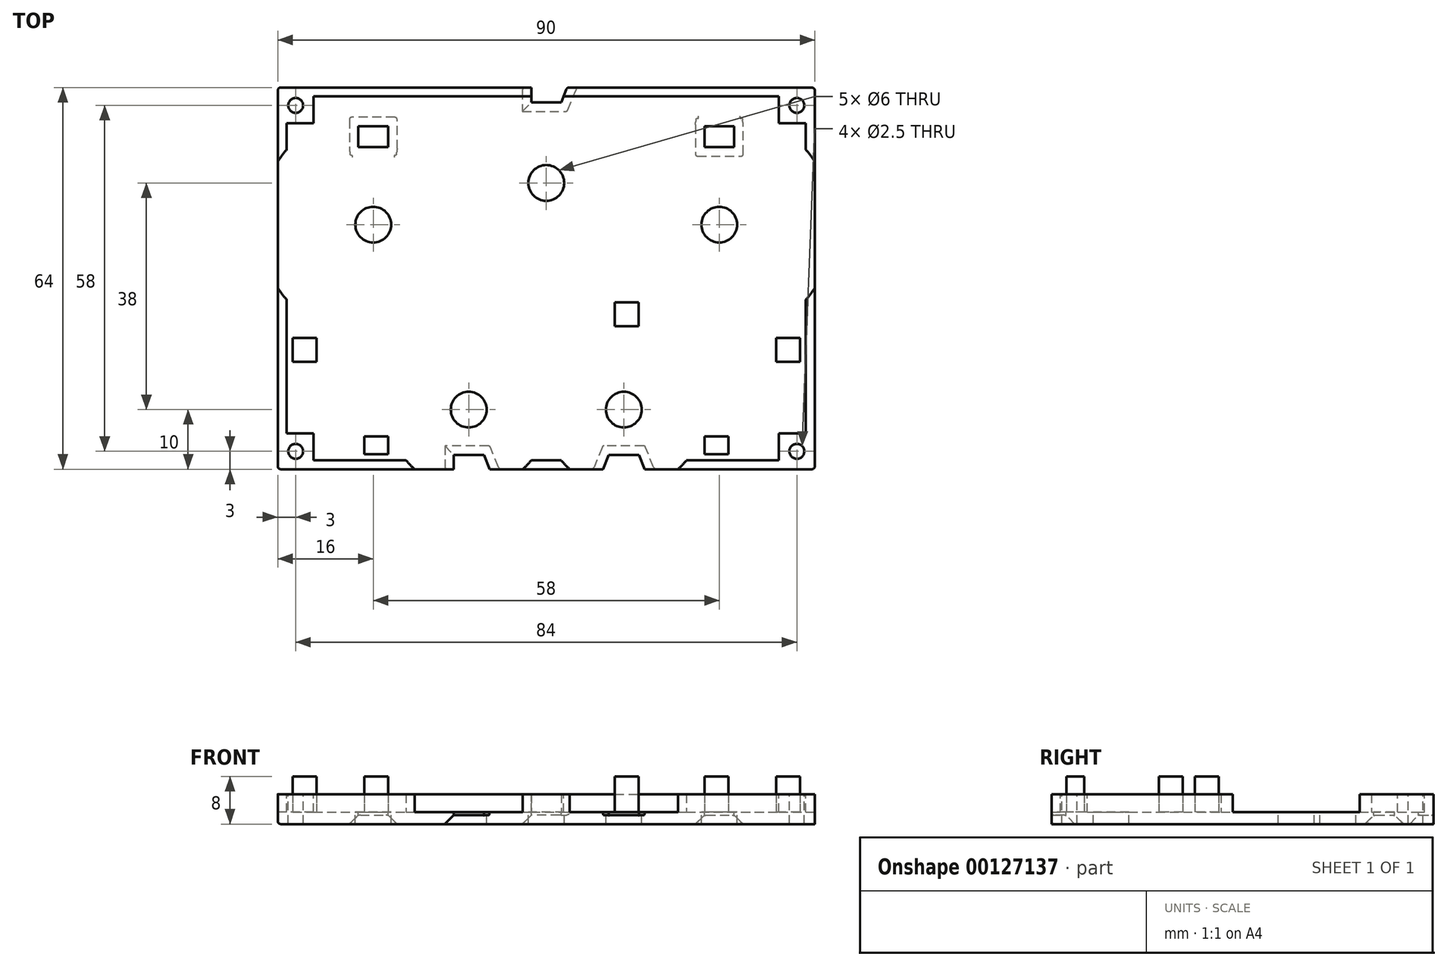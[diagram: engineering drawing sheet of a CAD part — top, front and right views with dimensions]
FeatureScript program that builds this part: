
annotation { "Feature Type Name" : "Feature", "Feature Type Description" : "" }
export const myFeature = defineFeature(function(context is Context, id is Id, definition is map)
    precondition{}
    {
        {
            var Q0;
            Q0=qCreatedBy(makeId("Top.planeOp"),FACE);
            var sketch = newSketch(context, id + "F0", { "sketchPlane" : qUnion([Q0])});
            skLineSegment(sketch, "E0.bottom", {"start": v(0, 0) * mm, "end": v(90, 0) * mm});
            skLineSegment(sketch, "E0.top", {"start": v(0, 64) * mm, "end": v(90, 64) * mm});
            skLineSegment(sketch, "E0.left", {"start": v(0, 0) * mm, "end": v(0, 64) * mm});
            skLineSegment(sketch, "E0.right", {"start": v(90, 0) * mm, "end": v(90, 64) * mm});
            skSolve(sketch);
        }
        {
            var Q0;
            Q0=makeQuery(id+"F0.imprint","IMPRINT",FACE,{"disambiguationData":[TD([[makeQuery(id+"F0.imprint","IMPRINT",EDGE,{"derivedFrom":sQuery(id+"F0.wireOp",EDGE,"E0.bottom")}),1.0]])]});
            extrude(context, id + "F1", {"entities" : qUnion([Q0]), "depth" : 2 * mm});
        }
        {
            var Q0;
            Q0=makeQuery(id+"F1.opExtrude","CAP_FACE",FACE,{"disambiguationData":[OSD([sQuery(id+"F0.wireOp",EDGE,"E0.bottom"),sQuery(id+"F0.wireOp",EDGE,"E0.top"),sQuery(id+"F0.wireOp",EDGE,"E0.left"),sQuery(id+"F0.wireOp",EDGE,"E0.right")])],"isStart":false});
            var sketch = newSketch(context, id + "F2", { "sketchPlane" : qUnion([Q0])});
            skCircle(sketch, "E1", {"center": v(16, 41) * mm, "radius": 18.2 * mm, "construction": true});
            skCircle(sketch, "E2", {"center": v(45, 48) * mm, "radius": 18.2 * mm, "construction": true});
            skCircle(sketch, "E3", {"center": v(74, 41) * mm, "radius": 18.2 * mm, "construction": true});
            skLineSegment(sketch, "E4", {"start": v(45, 64) * mm, "end": v(45, 0) * mm, "construction": true});
            skLineSegment(sketch, "E5", {"start": v(0, 41) * mm, "end": v(90, 41) * mm, "construction": true});
            skCircle(sketch, "E6", {"center": v(16, 41) * mm, "radius": 3 * mm, "construction": true});
            skCircle(sketch, "E7", {"center": v(45, 48) * mm, "radius": 3 * mm, "construction": true});
            skCircle(sketch, "E8", {"center": v(74, 41) * mm, "radius": 3 * mm, "construction": true});
            skCircle(sketch, "E9", {"center": v(32, 10) * mm, "radius": 12.5 * mm, "construction": true});
            skCircle(sketch, "E10", {"center": v(58, 10) * mm, "radius": 12.5 * mm, "construction": true});
            skLineSegment(sketch, "E11", {"start": v(32, 10) * mm, "end": v(58, 10) * mm, "construction": true});
            skPoint(sketch, "E12", {"position": v(45, 10) * mm});
            skSolve(sketch);
        }
        {
            var Q0;
            Q0=makeQuery(id+"F2.imprint","IMPRINT",FACE,{"disambiguationData":[TD([[makeQuery(id+"F2.imprint","IMPRINT",EDGE,{"derivedFrom":makeQuery(id+"F1.opExtrude","CAP_EDGE",EDGE,{"disambiguationData":[OSD([sQuery(id+"F0.wireOp",EDGE,"E0.bottom")])],"isStart":false})}),1.0]])]});
            var sketch = newSketch(context, id + "F3", { "sketchPlane" : qUnion([Q0])});
            skLineSegment(sketch, "E13.0", {"start": v(0, 0) * mm, "end": v(0, 64) * mm});
            skLineSegment(sketch, "E14.0", {"start": v(0, 0) * mm, "end": v(90, 0) * mm});
            skLineSegment(sketch, "E15.0", {"start": v(90, 0) * mm, "end": v(90, 64) * mm});
            skLineSegment(sketch, "E16.0", {"start": v(0, 64) * mm, "end": v(90, 64) * mm});
            skLineSegment(sketch, "E17.0", {"start": v(1.5, 62.5) * mm, "end": v(88.5, 62.5) * mm});
            skLineSegment(sketch, "E18.0", {"start": v(1.5, 1.5) * mm, "end": v(1.5, 62.5) * mm});
            skLineSegment(sketch, "E19.0", {"start": v(1.5, 1.5) * mm, "end": v(88.5, 1.5) * mm});
            skLineSegment(sketch, "E20.0", {"start": v(88.5, 1.5) * mm, "end": v(88.5, 62.5) * mm});
            skSolve(sketch);
        }
        {
            var Q0;
            Q0=makeQuery(id+"F3.imprint","IMPRINT",FACE,{"disambiguationData":[TD([[makeQuery(id+"F3.imprint","IMPRINT",EDGE,{"derivedFrom":sQuery(id+"F3.wireOp",EDGE,"E13.0")}),-1.0]])]});
            extrude(context, id + "F4", {"entities" : qUnion([Q0]), "operationType" : NewBodyOperationType.ADD, "depth" : 3 * mm});
        }
        {
            var Q0;
            Q0=makeQuery(id+"F2.imprint","IMPRINT",FACE,{"disambiguationData":[TD([[makeQuery(id+"F2.imprint","IMPRINT",EDGE,{"derivedFrom":makeQuery(id+"F1.opExtrude","CAP_EDGE",EDGE,{"disambiguationData":[OSD([sQuery(id+"F0.wireOp",EDGE,"E0.bottom")])],"isStart":false})}),1.0]])]});
            var sketch = newSketch(context, id + "F5", { "sketchPlane" : qUnion([Q0])});
            skCircle(sketch, "E21.0", {"center": v(16, 41) * mm, "radius": 19.2 * mm});
            skCircle(sketch, "E22.0", {"center": v(74, 41) * mm, "radius": 19.2 * mm});
            skCircle(sketch, "E23.0", {"center": v(32, 10) * mm, "radius": 13.5 * mm});
            skCircle(sketch, "E24.0", {"center": v(58, 10) * mm, "radius": 13.5 * mm});
            skSolve(sketch);
        }
        {
            var Q0;
            {var subQ0=sQuery(id+"F5.wireOp",EDGE,"E22.0");var subQ1=makeQuery(id+"F2.imprint","IMPRINT",EDGE,{"derivedFrom":makeQuery(id+"F1.opExtrude","CAP_EDGE",EDGE,{"disambiguationData":[OSD([sQuery(id+"F0.wireOp",EDGE,"E0.right")])],"isStart":false})});var subQ2=makeQuery(id+"F5.imprint","INTERSECT",VERTEX,{"disambiguationData":[OD(0.0)],"derivedFrom":[subQ1,subQ0]});Q0=makeQuery(id+"F5.imprint","IMPRINT",FACE,{"disambiguationData":[TD([[makeQuery(id+"F5.imprint","IMPRINT",EDGE,{"disambiguationData":[TD([[subQ2,1.0]])],"derivedFrom":subQ0}),1.0]])]});}
            var Q1;
            {var subQ0=sQuery(id+"F5.wireOp",EDGE,"E21.0");var subQ1=makeQuery(id+"F2.imprint","IMPRINT",EDGE,{"derivedFrom":makeQuery(id+"F1.opExtrude","CAP_EDGE",EDGE,{"disambiguationData":[OSD([sQuery(id+"F0.wireOp",EDGE,"E0.left")])],"isStart":false})});var subQ2=makeQuery(id+"F5.imprint","INTERSECT",VERTEX,{"disambiguationData":[OD(0.0)],"derivedFrom":[subQ1,subQ0]});Q1=makeQuery(id+"F5.imprint","IMPRINT",FACE,{"disambiguationData":[TD([[makeQuery(id+"F5.imprint","IMPRINT",EDGE,{"disambiguationData":[TD([[subQ2,-1.0]])],"derivedFrom":subQ0}),1.0]])]});}
            var Q2;
            {var subQ0=sQuery(id+"F5.wireOp",EDGE,"E23.0");var subQ1=makeQuery(id+"F2.imprint","IMPRINT",EDGE,{"derivedFrom":makeQuery(id+"F1.opExtrude","CAP_EDGE",EDGE,{"disambiguationData":[OSD([sQuery(id+"F0.wireOp",EDGE,"E0.bottom")])],"isStart":false})});var subQ2=makeQuery(id+"F5.imprint","INTERSECT",VERTEX,{"disambiguationData":[OD(0.0)],"derivedFrom":[subQ1,subQ0]});Q2=makeQuery(id+"F5.imprint","IMPRINT",FACE,{"disambiguationData":[TD([[makeQuery(id+"F5.imprint","IMPRINT",EDGE,{"disambiguationData":[TD([[subQ2,1.0]])],"derivedFrom":subQ0}),1.0]])]});}
            var Q3;
            {var subQ0=sQuery(id+"F5.wireOp",EDGE,"E23.0");var subQ1=makeQuery(id+"F2.imprint","IMPRINT",EDGE,{"derivedFrom":makeQuery(id+"F1.opExtrude","CAP_EDGE",EDGE,{"disambiguationData":[OSD([sQuery(id+"F0.wireOp",EDGE,"E0.bottom")])],"isStart":false})});var subQ2=makeQuery(id+"F5.imprint","INTERSECT",VERTEX,{"disambiguationData":[OD(0.0)],"derivedFrom":[subQ1,subQ0]});Q3=makeQuery(id+"F5.imprint","IMPRINT",FACE,{"disambiguationData":[TD([[makeQuery(id+"F5.imprint","IMPRINT",EDGE,{"disambiguationData":[TD([[subQ2,-1.0]])],"derivedFrom":subQ0}),1.0]])]});}
            var Q4;
            {var subQ0=sQuery(id+"F5.wireOp",EDGE,"E24.0");var subQ1=sQuery(id+"F5.wireOp",EDGE,"E23.0");var subQ2=makeQuery(id+"F5.imprint","INTERSECT",VERTEX,{"disambiguationData":[OD(0.0)],"derivedFrom":[subQ1,subQ0]});Q4=makeQuery(id+"F5.imprint","IMPRINT",FACE,{"disambiguationData":[TD([[makeQuery(id+"F5.imprint","IMPRINT",EDGE,{"disambiguationData":[TD([[subQ2,1.0]])],"derivedFrom":subQ1}),-1.0]])]});}
            extrude(context, id + "F6", {"entities" : qUnion([Q0, Q1, Q2, Q3, Q4]), "operationType" : NewBodyOperationType.REMOVE, "endBound" : BoundingType.THROUGH_ALL, "depth" : 25 * mm});
        }
        {
            var Q0;
            Q0=makeQuery(id+"F2.imprint","IMPRINT",FACE,{"disambiguationData":[TD([[makeQuery(id+"F2.imprint","IMPRINT",EDGE,{"derivedFrom":makeQuery(id+"F1.opExtrude","CAP_EDGE",EDGE,{"disambiguationData":[OSD([sQuery(id+"F0.wireOp",EDGE,"E0.bottom")])],"isStart":false})}),1.0]])]});
            var sketch = newSketch(context, id + "F7", { "sketchPlane" : qUnion([Q0])});
            skCircle(sketch, "E25", {"center": v(16, 41) * mm, "radius": 3 * mm});
            skCircle(sketch, "E26", {"center": v(45, 48) * mm, "radius": 3 * mm});
            skCircle(sketch, "E27", {"center": v(74, 41) * mm, "radius": 3 * mm});
            skCircle(sketch, "E28", {"center": v(32, 10) * mm, "radius": 3 * mm});
            skCircle(sketch, "E29", {"center": v(58, 10) * mm, "radius": 3 * mm});
            skSolve(sketch);
        }
        {
            var Q0;
            Q0=makeQuery(id+"F7.imprint","IMPRINT",FACE,{"disambiguationData":[TD([[makeQuery(id+"F7.imprint","IMPRINT",EDGE,{"derivedFrom":sQuery(id+"F7.wireOp",EDGE,"E26")}),1.0]])]});
            var Q1;
            Q1=makeQuery(id+"F7.imprint","IMPRINT",FACE,{"disambiguationData":[TD([[makeQuery(id+"F7.imprint","IMPRINT",EDGE,{"derivedFrom":sQuery(id+"F7.wireOp",EDGE,"E25")}),1.0]])]});
            var Q2;
            Q2=makeQuery(id+"F7.imprint","IMPRINT",FACE,{"disambiguationData":[TD([[makeQuery(id+"F7.imprint","IMPRINT",EDGE,{"derivedFrom":sQuery(id+"F7.wireOp",EDGE,"E27")}),1.0]])]});
            extrude(context, id + "F8", {"entities" : qUnion([Q0, Q1, Q2]), "operationType" : NewBodyOperationType.REMOVE, "endBound" : BoundingType.THROUGH_ALL, "oppositeDirection" : true, "depth" : 25 * mm});
        }
        {
            var Q0;
            Q0=makeQuery(id+"F7.imprint","IMPRINT",FACE,{"disambiguationData":[TD([[makeQuery(id+"F7.imprint","IMPRINT",EDGE,{"derivedFrom":sQuery(id+"F7.wireOp",EDGE,"E28")}),1.0]])]});
            var Q1;
            Q1=makeQuery(id+"F7.imprint","IMPRINT",FACE,{"disambiguationData":[TD([[makeQuery(id+"F7.imprint","IMPRINT",EDGE,{"derivedFrom":sQuery(id+"F7.wireOp",EDGE,"E29")}),1.0]])]});
            extrude(context, id + "F9", {"entities" : qUnion([Q0, Q1]), "operationType" : NewBodyOperationType.REMOVE, "endBound" : BoundingType.THROUGH_ALL, "oppositeDirection" : true, "depth" : 25 * mm});
        }
        {
            var Q0;
            Q0=makeQuery(id+"F2.imprint","IMPRINT",FACE,{"disambiguationData":[TD([[makeQuery(id+"F2.imprint","IMPRINT",EDGE,{"derivedFrom":makeQuery(id+"F1.opExtrude","CAP_EDGE",EDGE,{"disambiguationData":[OSD([sQuery(id+"F0.wireOp",EDGE,"E0.bottom")])],"isStart":false})}),1.0]])]});
            var sketch = newSketch(context, id + "F10", { "sketchPlane" : qUnion([Q0])});
            skLineSegment(sketch, "E30", {"start": v(76, 10) * mm, "end": v(58, 10) * mm, "construction": true});
            skPoint(sketch, "E31", {"position": v(19.5, 10) * mm});
            skPoint(sketch, "E32", {"position": v(70.5, 10) * mm});
            skLineSegment(sketch, "E33", {"start": v(45, 48) * mm, "end": v(45, 21.8) * mm, "construction": true});
            skPoint(sketch, "E34", {"position": v(45, 29.8) * mm});
            skLineSegment(sketch, "E35.bottom", {"start": v(42.5, 21.8) * mm, "end": v(47.5, 21.8) * mm});
            skLineSegment(sketch, "E35.top", {"start": v(42.5, 19.3) * mm, "end": v(47.5, 19.3) * mm, "construction": true});
            skLineSegment(sketch, "E35.left", {"start": v(42.5, 21.8) * mm, "end": v(42.5, 19.3) * mm});
            skLineSegment(sketch, "E35.right", {"start": v(47.5, 21.8) * mm, "end": v(47.5, 19.3) * mm});
            skLineSegment(sketch, "E36", {"start": v(45, 21.8) * mm, "end": v(45, 16.8) * mm, "construction": true});
            skPoint(sketch, "E36.endSnap0", {"position": v(45, 21.8) * mm});
            skLineSegment(sketch, "E37", {"start": v(45, 16.8) * mm, "end": v(47.5, 19.3) * mm});
            skLineSegment(sketch, "E38", {"start": v(42.5, 19.3) * mm, "end": v(45, 16.8) * mm});
            skLineSegment(sketch, "E39.bottom", {"start": v(44.5, 21.8) * mm, "end": v(45.5, 21.8) * mm});
            skLineSegment(sketch, "E39.top", {"start": v(44.5, 17.3) * mm, "end": v(45.5, 17.3) * mm});
            skLineSegment(sketch, "E39.left", {"start": v(44.5, 21.8) * mm, "end": v(44.5, 17.3) * mm});
            skLineSegment(sketch, "E39.right", {"start": v(45.5, 21.8) * mm, "end": v(45.5, 17.3) * mm});
            skLineSegment(sketch, "E40.0.0", {"start": v(0, 64) * mm, "end": v(0, 0) * mm, "construction": true});
            skLineSegment(sketch, "E40.0.1", {"start": v(0, 0) * mm, "end": v(90, 0) * mm, "construction": true});
            skLineSegment(sketch, "E40.0.2", {"start": v(90, 0) * mm, "end": v(90, 64) * mm, "construction": true});
            skLineSegment(sketch, "E40.0.3", {"start": v(90, 64) * mm, "end": v(0, 64) * mm, "construction": true});
            skLineSegment(sketch, "E41.0", {"start": v(1.5, 62.5) * mm, "end": v(88.5, 62.5) * mm, "construction": true});
            skLineSegment(sketch, "E42.bottom", {"start": v(80.5, 12.82) * mm, "end": v(85.5, 12.82) * mm, "construction": true});
            skLineSegment(sketch, "E42.top", {"start": v(80.5, 10.5) * mm, "end": v(85.5, 10.5) * mm});
            skLineSegment(sketch, "E42.left", {"start": v(80.5, 12.82) * mm, "end": v(80.5, 10.5) * mm});
            skLineSegment(sketch, "E42.right", {"start": v(85.5, 12.82) * mm, "end": v(85.5, 10.5) * mm, "construction": true});
            skLineSegment(sketch, "E43.MirrorCS", {"start": v(85.5, 7.18) * mm, "end": v(85.5, 9.5) * mm});
            skLineSegment(sketch, "E44.MirrorCS", {"start": v(80.5, 7.18) * mm, "end": v(80.5, 9.5) * mm});
            skLineSegment(sketch, "E45.MirrorCS", {"start": v(80.5, 7.18) * mm, "end": v(85.5, 7.18) * mm});
            skLineSegment(sketch, "E46.MirrorCS", {"start": v(80.5, 9.5) * mm, "end": v(85.5, 9.5) * mm});
            skLineSegment(sketch, "E47", {"start": v(74, 41) * mm, "end": v(83.82, 14.03) * mm, "construction": true});
            skPoint(sketch, "E48", {"position": v(80.22, 23.9) * mm});
            skPoint(sketch, "E49.endSnap0", {"position": v(47.5, 20.55) * mm});
            skLineSegment(sketch, "E50", {"start": v(83.35, 13.86) * mm, "end": v(88.5, 15.74) * mm, "construction": true});
            skLineSegment(sketch, "E51.0", {"start": v(88.5, 1.5) * mm, "end": v(88.5, 28.41) * mm, "construction": true});
            skLineSegment(sketch, "E52", {"start": v(84.29, 14.2) * mm, "end": v(88.5, 15.74) * mm});
            skLineSegment(sketch, "E53", {"start": v(88.5, 15.74) * mm, "end": v(88.5, 3.62) * mm});
            skLineSegment(sketch, "E54", {"start": v(83.35, 13.86) * mm, "end": v(84.57, 10.5) * mm});
            skLineSegment(sketch, "E55", {"start": v(83.35, 13.86) * mm, "end": v(80.5, 12.82) * mm});
            skLineSegment(sketch, "E56", {"start": v(84.57, 10.5) * mm, "end": v(85.5, 10.5) * mm});
            skLineSegment(sketch, "E57.MirrorCS", {"start": v(0, 0) * mm, "end": v(0, 64) * mm, "construction": true});
            skPoint(sketch, "E58.MirrorP", {"position": v(9.78, 23.9) * mm});
            skLineSegment(sketch, "E59", {"start": v(88.5, 10.5) * mm, "end": v(85.63, 10.5) * mm});
            skLineSegment(sketch, "E60", {"start": v(84.29, 14.2) * mm, "end": v(85.63, 10.5) * mm});
            skLineSegment(sketch, "E61", {"start": v(88.25, 15.64) * mm, "end": v(88.25, 10.5) * mm});
            skLineSegment(sketch, "E62.MirrorCS", {"start": v(5.43, 10.5) * mm, "end": v(4.5, 10.5) * mm});
            skLineSegment(sketch, "E63.MirrorCS", {"start": v(5.71, 14.2) * mm, "end": v(1.5, 15.74) * mm});
            skLineSegment(sketch, "E64.MirrorCS", {"start": v(1.5, 15.74) * mm, "end": v(1.5, 3.62) * mm});
            skLineSegment(sketch, "E65.MirrorCS", {"start": v(16, 41) * mm, "end": v(6.18, 14.03) * mm, "construction": true});
            skLineSegment(sketch, "E66.MirrorCS", {"start": v(6.65, 13.86) * mm, "end": v(9.5, 12.82) * mm});
            skLineSegment(sketch, "E67.MirrorCS", {"start": v(6.65, 13.86) * mm, "end": v(1.5, 15.74) * mm, "construction": true});
            skLineSegment(sketch, "E68.MirrorCS", {"start": v(9.5, 7.18) * mm, "end": v(4.5, 7.18) * mm});
            skLineSegment(sketch, "E69.MirrorCS", {"start": v(9.5, 10.5) * mm, "end": v(4.5, 10.5) * mm});
            skLineSegment(sketch, "E70.MirrorCS", {"start": v(5.71, 14.2) * mm, "end": v(4.37, 10.5) * mm});
            skLineSegment(sketch, "E71.MirrorCS", {"start": v(9.5, 12.82) * mm, "end": v(9.5, 10.5) * mm});
            skLineSegment(sketch, "E72.MirrorCS", {"start": v(9.5, 7.18) * mm, "end": v(9.5, 9.5) * mm});
            skLineSegment(sketch, "E73.MirrorCS", {"start": v(1.5, 1.5) * mm, "end": v(1.5, 28.41) * mm, "construction": true});
            skLineSegment(sketch, "E74.MirrorCS", {"start": v(1.75, 15.64) * mm, "end": v(1.75, 10.5) * mm});
            skLineSegment(sketch, "E75.MirrorCS", {"start": v(4.5, 12.82) * mm, "end": v(4.5, 10.5) * mm, "construction": true});
            skLineSegment(sketch, "E76.MirrorCS", {"start": v(90, 0) * mm, "end": v(0, 0) * mm, "construction": true});
            skLineSegment(sketch, "E77.MirrorCS", {"start": v(14, 10) * mm, "end": v(32, 10) * mm, "construction": true});
            skLineSegment(sketch, "E78.MirrorCS", {"start": v(9.5, 12.82) * mm, "end": v(4.5, 12.82) * mm, "construction": true});
            skLineSegment(sketch, "E79.MirrorCS", {"start": v(6.65, 13.86) * mm, "end": v(5.43, 10.5) * mm});
            skLineSegment(sketch, "E80.MirrorCS", {"start": v(4.5, 7.18) * mm, "end": v(4.5, 9.5) * mm});
            skLineSegment(sketch, "E81.MirrorCS", {"start": v(9.5, 9.5) * mm, "end": v(4.5, 9.5) * mm});
            skLineSegment(sketch, "E82.MirrorCS", {"start": v(1.5, 10.5) * mm, "end": v(4.37, 10.5) * mm});
            skSolve(sketch);
        }
        {
            var Q0;
            {var subQ0=sQuery(id+"F3.wireOp",EDGE,"E14.0");var subQ1=sQuery(id+"F3.wireOp",EDGE,"E13.0");var subQ2=sQuery(id+"F3.wireOp",EDGE,"E18.0");var subQ3=sQuery(id+"F0.wireOp",EDGE,"E0.bottom");var subQ4=sQuery(id+"F3.wireOp",EDGE,"E19.0");var subQ5=sQuery(id+"F5.wireOp",EDGE,"E24.0");var subQ6=sQuery(id+"F5.wireOp",EDGE,"E23.0");var subQ7=makeQuery(id+"F2.imprint","IMPRINT",EDGE,{"derivedFrom":makeQuery(id+"F1.opExtrude","CAP_EDGE",EDGE,{"disambiguationData":[OSD([subQ3])],"isStart":false})});var subQ9=makeQuery(id+"F5.imprint","INTERSECT",VERTEX,{"disambiguationData":[OD(0.0)],"derivedFrom":[subQ7,subQ6]});Q0=makeQuery(id+"F6.boolean.opBoolean","SPLIT",FACE,{"disambiguationData":[TD([makeQuery(id+"F1.opExtrude","SWEPT_FACE",FACE,{"disambiguationData":[OSD([subQ3])]}),makeQuery(id+"F1.opExtrude","SWEPT_FACE",FACE,{"disambiguationData":[OSD([sQuery(id+"F0.wireOp",EDGE,"E0.left")])]}),makeQuery(id+"F4.opExtrude","SWEPT_FACE",FACE,{"disambiguationData":[OSD([subQ1])]}),makeQuery(id+"F4.opExtrude","SWEPT_FACE",FACE,{"disambiguationData":[OSD([subQ0])]}),makeQuery(id+"F4.opExtrude","SWEPT_FACE",FACE,{"disambiguationData":[OSD([subQ2])]}),makeQuery(id+"F4.opExtrude","SWEPT_FACE",FACE,{"disambiguationData":[OSD([subQ4])]}),makeQuery(id+"F6.opExtrude","SWEPT_FACE",FACE,{"disambiguationData":[OSD([sQuery(id+"F5.wireOp",EDGE,"E21.0")])]}),makeQuery(id+"F6.opExtrude","SWEPT_FACE",FACE,{"disambiguationData":[OSD([subQ6]),TDD([makeQuery(id+"F5.imprint","IMPRINT",EDGE,{"disambiguationData":[TD([[makeQuery(id+"F5.imprint","INTERSECT",VERTEX,{"disambiguationData":[OD(0.0)],"derivedFrom":[subQ6,subQ5]}),-1.0]])],"derivedFrom":subQ6}),makeQuery(id+"F5.imprint","IMPRINT",EDGE,{"disambiguationData":[TD([[subQ9,-1.0]])],"derivedFrom":subQ6}),makeQuery(id+"F5.imprint","IMPRINT",EDGE,{"disambiguationData":[TD([[makeQuery(id+"F5.imprint","INTERSECT",VERTEX,{"disambiguationData":[OD(1.0)],"derivedFrom":[subQ6,subQ5]}),1.0]])],"derivedFrom":subQ6})])]})])],"derivedFrom":makeQuery(id+"F4.opExtrude","CAP_FACE",FACE,{"disambiguationData":[OSD([subQ1,subQ0,sQuery(id+"F3.wireOp",EDGE,"E15.0"),sQuery(id+"F3.wireOp",EDGE,"E16.0"),sQuery(id+"F3.wireOp",EDGE,"E17.0"),subQ2,subQ4,sQuery(id+"F3.wireOp",EDGE,"E20.0")])],"isStart":false})});}
            var sketch = newSketch(context, id + "F11", { "sketchPlane" : qUnion([Q0])});
            skLineSegment(sketch, "E83.0", {"start": v(1.5, 1.5) * mm, "end": v(1.5, 28.41) * mm});
            skLineSegment(sketch, "E83.1", {"start": v(1.5, 1.5) * mm, "end": v(21.51, 1.5) * mm});
            skLineSegment(sketch, "E83.2", {"start": v(88.5, 53.59) * mm, "end": v(88.5, 62.5) * mm});
            skLineSegment(sketch, "E83.3", {"start": v(1.5, 62.5) * mm, "end": v(88.5, 62.5) * mm});
            skLineSegment(sketch, "E83.4", {"start": v(1.5, 53.59) * mm, "end": v(1.5, 62.5) * mm});
            skLineSegment(sketch, "E83.5", {"start": v(88.5, 1.5) * mm, "end": v(88.5, 28.41) * mm});
            skLineSegment(sketch, "E83.6", {"start": v(68.49, 1.5) * mm, "end": v(88.5, 1.5) * mm});
            skLineSegment(sketch, "E84.bottom", {"start": v(1.5, 1.5) * mm, "end": v(6, 1.5) * mm});
            skLineSegment(sketch, "E84.top", {"start": v(1.5, 6) * mm, "end": v(6, 6) * mm});
            skLineSegment(sketch, "E84.left", {"start": v(1.5, 1.5) * mm, "end": v(1.5, 6) * mm});
            skLineSegment(sketch, "E84.right", {"start": v(6, 1.5) * mm, "end": v(6, 6) * mm});
            skLineSegment(sketch, "E85.bottom", {"start": v(1.5, 62.5) * mm, "end": v(6, 62.5) * mm});
            skLineSegment(sketch, "E85.top", {"start": v(1.5, 58) * mm, "end": v(6, 58) * mm});
            skLineSegment(sketch, "E85.left", {"start": v(1.5, 62.5) * mm, "end": v(1.5, 58) * mm});
            skLineSegment(sketch, "E85.right", {"start": v(6, 62.5) * mm, "end": v(6, 58) * mm});
            skLineSegment(sketch, "E86.bottom", {"start": v(88.5, 1.5) * mm, "end": v(84, 1.5) * mm});
            skLineSegment(sketch, "E86.top", {"start": v(88.5, 6) * mm, "end": v(84, 6) * mm});
            skLineSegment(sketch, "E86.left", {"start": v(88.5, 1.5) * mm, "end": v(88.5, 6) * mm});
            skLineSegment(sketch, "E86.right", {"start": v(84, 1.5) * mm, "end": v(84, 6) * mm});
            skLineSegment(sketch, "E87.bottom", {"start": v(88.5, 62.5) * mm, "end": v(84, 62.5) * mm});
            skLineSegment(sketch, "E87.top", {"start": v(88.5, 58) * mm, "end": v(84, 58) * mm});
            skLineSegment(sketch, "E87.left", {"start": v(88.5, 62.5) * mm, "end": v(88.5, 58) * mm});
            skLineSegment(sketch, "E87.right", {"start": v(84, 62.5) * mm, "end": v(84, 58) * mm});
            skCircle(sketch, "E88", {"center": v(3, 3) * mm, "radius": 1.25 * mm});
            skCircle(sketch, "E89", {"center": v(3, 61) * mm, "radius": 1.25 * mm});
            skCircle(sketch, "E90", {"center": v(87, 61) * mm, "radius": 1.25 * mm});
            skCircle(sketch, "E91", {"center": v(87, 3) * mm, "radius": 1.25 * mm});
            skSolve(sketch);
        }
        {
            var Q0;
            Q0 = qSketchRegion(id + "F11", true);
            extrude(context, id + "F12", {"entities" : qUnion([Q0]), "operationType" : NewBodyOperationType.ADD, "endBound" : BoundingType.UP_TO_NEXT, "oppositeDirection" : true, "depth" : 25 * mm});
        }
        {
            var Q0;
            {var subQ0=sQuery(id+"F3.wireOp",EDGE,"E20.0");var subQ1=sQuery(id+"F3.wireOp",EDGE,"E17.0");var subQ2=sQuery(id+"F3.wireOp",EDGE,"E15.0");var subQ3=sQuery(id+"F3.wireOp",EDGE,"E16.0");var subQ4=sQuery(id+"F3.wireOp",EDGE,"E18.0");var subQ5=sQuery(id+"F3.wireOp",EDGE,"E13.0");Q0=makeQuery(id+"F12.boolean.opBoolean","MERGE",FACE,{"derivedFrom":[makeQuery(id+"F6.boolean.opBoolean","SPLIT",FACE,{"disambiguationData":[TD([makeQuery(id+"F1.opExtrude","SWEPT_FACE",FACE,{"disambiguationData":[OSD([sQuery(id+"F0.wireOp",EDGE,"E0.top")])]}),makeQuery(id+"F1.opExtrude","SWEPT_FACE",FACE,{"disambiguationData":[OSD([sQuery(id+"F0.wireOp",EDGE,"E0.left")])]}),makeQuery(id+"F1.opExtrude","SWEPT_FACE",FACE,{"disambiguationData":[OSD([sQuery(id+"F0.wireOp",EDGE,"E0.right")])]}),makeQuery(id+"F4.opExtrude","SWEPT_FACE",FACE,{"disambiguationData":[OSD([subQ5])]}),makeQuery(id+"F4.opExtrude","SWEPT_FACE",FACE,{"disambiguationData":[OSD([subQ2])]}),makeQuery(id+"F4.opExtrude","SWEPT_FACE",FACE,{"disambiguationData":[OSD([subQ3])]}),makeQuery(id+"F4.opExtrude","SWEPT_FACE",FACE,{"disambiguationData":[OSD([subQ1])]}),makeQuery(id+"F4.opExtrude","SWEPT_FACE",FACE,{"disambiguationData":[OSD([subQ4])]}),makeQuery(id+"F4.opExtrude","SWEPT_FACE",FACE,{"disambiguationData":[OSD([subQ0])]}),makeQuery(id+"F6.opExtrude","SWEPT_FACE",FACE,{"disambiguationData":[OSD([sQuery(id+"F5.wireOp",EDGE,"E21.0")])]}),makeQuery(id+"F6.opExtrude","SWEPT_FACE",FACE,{"disambiguationData":[OSD([sQuery(id+"F5.wireOp",EDGE,"E22.0")])]})])],"derivedFrom":makeQuery(id+"F4.opExtrude","CAP_FACE",FACE,{"disambiguationData":[OSD([subQ5,sQuery(id+"F3.wireOp",EDGE,"E14.0"),subQ2,subQ3,subQ1,subQ4,sQuery(id+"F3.wireOp",EDGE,"E19.0"),subQ0])],"isStart":false})}),makeQuery(id+"F12.opExtrude","CAP_FACE",FACE,{"disambiguationData":[OSD([sQuery(id+"F11.wireOp",EDGE,"E85.bottom"),sQuery(id+"F11.wireOp",EDGE,"E85.top"),sQuery(id+"F11.wireOp",EDGE,"E85.left"),sQuery(id+"F11.wireOp",EDGE,"E85.right")])],"isStart":true}),makeQuery(id+"F12.opExtrude","CAP_FACE",FACE,{"disambiguationData":[OSD([sQuery(id+"F11.wireOp",EDGE,"E87.bottom"),sQuery(id+"F11.wireOp",EDGE,"E87.top"),sQuery(id+"F11.wireOp",EDGE,"E87.left"),sQuery(id+"F11.wireOp",EDGE,"E87.right")])],"isStart":true})]});}
            var sketch = newSketch(context, id + "F13", { "sketchPlane" : qUnion([Q0])});
            skCircle(sketch, "E92.0", {"center": v(3, 61) * mm, "radius": 1.25 * mm});
            skCircle(sketch, "E93.0", {"center": v(3, 3) * mm, "radius": 1.25 * mm});
            skCircle(sketch, "E94.0", {"center": v(87, 3) * mm, "radius": 1.25 * mm});
            skCircle(sketch, "E95.0", {"center": v(87, 61) * mm, "radius": 1.25 * mm});
            skSolve(sketch);
        }
        {
            var Q0;
            Q0 = qSketchRegion(id + "F13", true);
            extrude(context, id + "F14", {"entities" : qUnion([Q0]), "operationType" : NewBodyOperationType.REMOVE, "endBound" : BoundingType.THROUGH_ALL, "oppositeDirection" : true, "depth" : 25 * mm});
        }
        {
            var Q0;
            Q0=makeQuery(id+"F2.imprint","IMPRINT",FACE,{"disambiguationData":[TD([[makeQuery(id+"F2.imprint","IMPRINT",EDGE,{"derivedFrom":makeQuery(id+"F1.opExtrude","CAP_EDGE",EDGE,{"disambiguationData":[OSD([sQuery(id+"F0.wireOp",EDGE,"E0.bottom")])],"isStart":false})}),1.0]])]});
            var sketch = newSketch(context, id + "F15", { "sketchPlane" : qUnion([Q0])});
            skLineSegment(sketch, "E96.0", {"start": v(32, 10) * mm, "end": v(58, 10) * mm, "construction": true});
            skLineSegment(sketch, "E97.0", {"start": v(45, 64) * mm, "end": v(45, 0) * mm, "construction": true});
            skLineSegment(sketch, "E98.0", {"start": v(0, 41) * mm, "end": v(90, 41) * mm, "construction": true});
            skLineSegment(sketch, "E99", {"start": v(32, 10) * mm, "end": v(32, -0.6) * mm, "construction": true});
            skLineSegment(sketch, "E100.bottom", {"start": v(29.5, 2.4) * mm, "end": v(34.5, 2.4) * mm});
            skLineSegment(sketch, "E100.top", {"start": v(29.5, -0.6) * mm, "end": v(34.5, -0.6) * mm});
            skLineSegment(sketch, "E100.left", {"start": v(29.5, 2.4) * mm, "end": v(29.5, -0.6) * mm});
            skLineSegment(sketch, "E100.right", {"start": v(34.5, 2.4) * mm, "end": v(34.5, -0.6) * mm});
            skLineSegment(sketch, "E101", {"start": v(16, 41) * mm, "end": v(16, 57.5) * mm, "construction": true});
            skLineSegment(sketch, "E102.bottom", {"start": v(13.5, 57.5) * mm, "end": v(18.5, 57.5) * mm});
            skLineSegment(sketch, "E102.top", {"start": v(13.5, 54) * mm, "end": v(18.5, 54) * mm});
            skLineSegment(sketch, "E102.left", {"start": v(13.5, 57.5) * mm, "end": v(13.5, 54) * mm});
            skLineSegment(sketch, "E102.right", {"start": v(18.5, 57.5) * mm, "end": v(18.5, 54) * mm});
            skLineSegment(sketch, "E103", {"start": v(45, 48) * mm, "end": v(45, 65) * mm, "construction": true});
            skLineSegment(sketch, "E104.bottom", {"start": v(42.5, 65) * mm, "end": v(47.5, 65) * mm});
            skLineSegment(sketch, "E104.top", {"start": v(42.5, 61.5) * mm, "end": v(47.5, 61.5) * mm});
            skLineSegment(sketch, "E104.left", {"start": v(42.5, 65) * mm, "end": v(42.5, 61.5) * mm});
            skLineSegment(sketch, "E104.right", {"start": v(47.5, 65) * mm, "end": v(47.5, 61.5) * mm});
            skLineSegment(sketch, "E105.MirrorCS", {"start": v(71.5, 57.5) * mm, "end": v(71.5, 54) * mm});
            skLineSegment(sketch, "E106.MirrorCS", {"start": v(76.5, 54) * mm, "end": v(71.5, 54) * mm});
            skLineSegment(sketch, "E107.MirrorCS", {"start": v(76.5, 57.5) * mm, "end": v(76.5, 54) * mm});
            skLineSegment(sketch, "E108.MirrorCS", {"start": v(76.5, 57.5) * mm, "end": v(71.5, 57.5) * mm});
            skLineSegment(sketch, "E109.MirrorCS", {"start": v(60.5, 2.4) * mm, "end": v(55.5, 2.4) * mm});
            skLineSegment(sketch, "E110.MirrorCS", {"start": v(60.5, -0.6) * mm, "end": v(55.5, -0.6) * mm});
            skLineSegment(sketch, "E111.MirrorCS", {"start": v(60.5, 2.4) * mm, "end": v(60.5, -0.6) * mm});
            skLineSegment(sketch, "E112.MirrorCS", {"start": v(55.5, 2.4) * mm, "end": v(55.5, -0.6) * mm});
            skLineSegment(sketch, "E113.MirrorCS", {"start": v(58, 10) * mm, "end": v(58, -0.6) * mm, "construction": true});
            skSolve(sketch);
        }
        {
            var Q0;
            Q0=makeQuery(id+"F15.imprint","IMPRINT",FACE,{"disambiguationData":[TD([[makeQuery(id+"F15.imprint","IMPRINT",EDGE,{"derivedFrom":sQuery(id+"F15.wireOp",EDGE,"E102.bottom")}),-1.0]])]});
            var Q1;
            {var subQ0=sQuery(id+"F15.wireOp",EDGE,"E104.top");Q1=makeQuery(id+"F15.imprint","IMPRINT",FACE,{"disambiguationData":[TD([[makeQuery(id+"F15.imprint","IMPRINT",EDGE,{"derivedFrom":subQ0}),1.0]])]});}
            var Q2;
            Q2=makeQuery(id+"F15.imprint","IMPRINT",FACE,{"disambiguationData":[TD([[makeQuery(id+"F15.imprint","IMPRINT",EDGE,{"derivedFrom":sQuery(id+"F15.wireOp",EDGE,"E105.MirrorCS")}),1.0]])]});
            var Q3;
            {var subQ0=sQuery(id+"F15.wireOp",EDGE,"E109.MirrorCS");Q3=makeQuery(id+"F15.imprint","IMPRINT",FACE,{"disambiguationData":[TD([[makeQuery(id+"F15.imprint","IMPRINT",EDGE,{"derivedFrom":subQ0}),1.0]])]});}
            var Q4;
            {var subQ0=sQuery(id+"F15.wireOp",EDGE,"E100.bottom");Q4=makeQuery(id+"F15.imprint","IMPRINT",FACE,{"disambiguationData":[TD([[makeQuery(id+"F15.imprint","IMPRINT",EDGE,{"derivedFrom":subQ0}),-1.0]])]});}
            extrude(context, id + "F16", {"entities" : qUnion([Q0, Q1, Q2, Q3, Q4]), "operationType" : NewBodyOperationType.REMOVE, "endBound" : BoundingType.THROUGH_ALL, "oppositeDirection" : true, "depth" : 25 * mm, "hasSecondDirection" : true, "secondDirectionBound" : SecondDirectionBoundingType.THROUGH_ALL, "secondDirectionOppositeDirection" : false, "secondDirectionDepth" : 25 * mm});
        }
        {
            var Q0;
            {var subQ12=sQuery(id+"F10.wireOp",EDGE,"E35.left");Q0=makeQuery(id+"F10.imprint","IMPRINT",FACE,{"disambiguationData":[TD([[makeQuery(id+"F10.imprint","IMPRINT",EDGE,{"derivedFrom":subQ12}),-1.0]])]});}
            var sketch = newSketch(context, id + "F17", { "sketchPlane" : qUnion([Q0])});
            skLineSegment(sketch, "E114", {"start": v(42.5, 28.2) * mm, "end": v(42.9, 28.2) * mm, "construction": true});
            skLineSegment(sketch, "E115", {"start": v(42.9, 28.2) * mm, "end": v(45, 30.82) * mm, "construction": true});
            skLineSegment(sketch, "E116", {"start": v(45, 30.82) * mm, "end": v(47.1, 28.2) * mm, "construction": true});
            skLineSegment(sketch, "E117", {"start": v(47.1, 28.2) * mm, "end": v(62.5, 28.2) * mm, "construction": true});
            skLineSegment(sketch, "E118", {"start": v(62.5, 28.2) * mm, "end": v(62.5, 28) * mm, "construction": true});
            skLineSegment(sketch, "E119", {"start": v(62.5, 28) * mm, "end": v(47, 28) * mm, "construction": true});
            skLineSegment(sketch, "E120", {"start": v(47, 28) * mm, "end": v(45, 30.5) * mm, "construction": true});
            skLineSegment(sketch, "E121", {"start": v(45, 30.5) * mm, "end": v(43, 28) * mm, "construction": true});
            skLineSegment(sketch, "E122", {"start": v(43, 28) * mm, "end": v(42.5, 28) * mm, "construction": true});
            skLineSegment(sketch, "E123", {"start": v(42.5, 28) * mm, "end": v(42.5, 28.2) * mm, "construction": true});
            skLineSegment(sketch, "E124.0", {"start": v(45, 64) * mm, "end": v(45, 0) * mm, "construction": true});
            skLineSegment(sketch, "E125.bottom", {"start": v(60.5, 28) * mm, "end": v(56.5, 28) * mm});
            skLineSegment(sketch, "E125.top", {"start": v(60.5, 24) * mm, "end": v(56.5, 24) * mm});
            skLineSegment(sketch, "E125.left", {"start": v(60.5, 28) * mm, "end": v(60.5, 24) * mm});
            skLineSegment(sketch, "E125.right", {"start": v(56.5, 28) * mm, "end": v(56.5, 24) * mm});
            skLineSegment(sketch, "E126.bottom", {"start": v(-1.53, 22.2) * mm, "end": v(17.97, 22.2) * mm, "construction": true});
            skLineSegment(sketch, "E126.top", {"start": v(-1.53, 22) * mm, "end": v(17.97, 22) * mm, "construction": true});
            skLineSegment(sketch, "E126.left", {"start": v(-1.53, 22.2) * mm, "end": v(-1.53, 22) * mm, "construction": true});
            skLineSegment(sketch, "E126.right", {"start": v(17.97, 22.2) * mm, "end": v(17.97, 22) * mm, "construction": true});
            skLineSegment(sketch, "E127", {"start": v(13.47, 22.2) * mm, "end": v(15.72, 24.5) * mm, "construction": true});
            skLineSegment(sketch, "E128", {"start": v(15.72, 24.5) * mm, "end": v(17.97, 22.2) * mm, "construction": true});
            skLineSegment(sketch, "E129", {"start": v(15.72, 24.5) * mm, "end": v(15.72, 22) * mm, "construction": true});
            skLineSegment(sketch, "E130.0", {"start": v(1.5, 1.5) * mm, "end": v(1.5, 28.41) * mm, "construction": true});
            skLineSegment(sketch, "E131.bottom", {"start": v(1.5, 22) * mm, "end": v(6.5, 22) * mm});
            skLineSegment(sketch, "E131.top", {"start": v(1.5, 18) * mm, "end": v(6.5, 18) * mm});
            skLineSegment(sketch, "E131.right", {"start": v(6.5, 22) * mm, "end": v(6.5, 18) * mm});
            skLineSegment(sketch, "E132", {"start": v(2.5, 22) * mm, "end": v(2.5, 18) * mm});
            skLineSegment(sketch, "E133.MirrorCS", {"start": v(72.03, 22.2) * mm, "end": v(72.03, 22) * mm, "construction": true});
            skLineSegment(sketch, "E134.MirrorCS", {"start": v(91.53, 22.2) * mm, "end": v(91.53, 22) * mm, "construction": true});
            skLineSegment(sketch, "E135.MirrorCS", {"start": v(88.5, 22) * mm, "end": v(83.5, 22) * mm});
            skLineSegment(sketch, "E136.MirrorCS", {"start": v(76.53, 22.2) * mm, "end": v(74.28, 24.5) * mm, "construction": true});
            skLineSegment(sketch, "E137.MirrorCS", {"start": v(83.5, 22) * mm, "end": v(83.5, 18) * mm});
            skLineSegment(sketch, "E138.MirrorCS", {"start": v(87.5, 22) * mm, "end": v(87.5, 18) * mm});
            skLineSegment(sketch, "E139.MirrorCS", {"start": v(74.28, 24.5) * mm, "end": v(74.28, 22) * mm, "construction": true});
            skLineSegment(sketch, "E140.MirrorCS", {"start": v(91.53, 22.2) * mm, "end": v(72.03, 22.2) * mm, "construction": true});
            skLineSegment(sketch, "E141.MirrorCS", {"start": v(91.53, 22) * mm, "end": v(72.03, 22) * mm, "construction": true});
            skLineSegment(sketch, "E142.MirrorCS", {"start": v(74.28, 24.5) * mm, "end": v(72.03, 22.2) * mm, "construction": true});
            skLineSegment(sketch, "E143.MirrorCS", {"start": v(88.5, 18) * mm, "end": v(83.5, 18) * mm});
            skLineSegment(sketch, "E144.bottom", {"start": v(18.5, 2.25) * mm, "end": v(18.6, 2.25) * mm, "construction": true});
            skLineSegment(sketch, "E144.top", {"start": v(18.5, 12.25) * mm, "end": v(18.6, 12.25) * mm, "construction": true});
            skLineSegment(sketch, "E144.left", {"start": v(18.5, 2.25) * mm, "end": v(18.5, 12.25) * mm, "construction": true});
            skLineSegment(sketch, "E144.right", {"start": v(18.6, 2.25) * mm, "end": v(18.6, 12.25) * mm, "construction": true});
            skLineSegment(sketch, "E145.0", {"start": v(6, 1.5) * mm, "end": v(21.51, 1.5) * mm, "construction": true});
            skLineSegment(sketch, "E146", {"start": v(18.6, 12.25) * mm, "end": v(21, 10) * mm, "construction": true});
            skLineSegment(sketch, "E147", {"start": v(21, 10) * mm, "end": v(18.6, 7.75) * mm, "construction": true});
            skLineSegment(sketch, "E148", {"start": v(21, 10) * mm, "end": v(18.5, 10) * mm, "construction": true});
            skLineSegment(sketch, "E149.bottom", {"start": v(14.5, 5.5) * mm, "end": v(18.5, 5.5) * mm});
            skLineSegment(sketch, "E149.top", {"start": v(14.5, 2.5) * mm, "end": v(18.5, 2.5) * mm});
            skLineSegment(sketch, "E149.left", {"start": v(14.5, 5.5) * mm, "end": v(14.5, 2.5) * mm});
            skLineSegment(sketch, "E149.right", {"start": v(18.5, 5.5) * mm, "end": v(18.5, 2.5) * mm});
            skLineSegment(sketch, "E150.MirrorCS", {"start": v(71.5, 12.25) * mm, "end": v(71.4, 12.25) * mm, "construction": true});
            skLineSegment(sketch, "E151.MirrorCS", {"start": v(71.5, 2.25) * mm, "end": v(71.4, 2.25) * mm, "construction": true});
            skLineSegment(sketch, "E152.MirrorCS", {"start": v(71.5, 5.5) * mm, "end": v(71.5, 2.5) * mm});
            skLineSegment(sketch, "E153.MirrorCS", {"start": v(75.5, 2.5) * mm, "end": v(71.5, 2.5) * mm});
            skLineSegment(sketch, "E154.MirrorCS", {"start": v(71.5, 2.25) * mm, "end": v(71.5, 12.25) * mm, "construction": true});
            skLineSegment(sketch, "E155.MirrorCS", {"start": v(69, 10) * mm, "end": v(71.4, 7.75) * mm, "construction": true});
            skLineSegment(sketch, "E156.MirrorCS", {"start": v(84, 1.5) * mm, "end": v(68.49, 1.5) * mm, "construction": true});
            skLineSegment(sketch, "E157.MirrorCS", {"start": v(75.5, 5.5) * mm, "end": v(71.5, 5.5) * mm});
            skLineSegment(sketch, "E158.MirrorCS", {"start": v(71.4, 12.25) * mm, "end": v(69, 10) * mm, "construction": true});
            skLineSegment(sketch, "E159.MirrorCS", {"start": v(75.5, 5.5) * mm, "end": v(75.5, 2.5) * mm});
            skLineSegment(sketch, "E160.MirrorCS", {"start": v(69, 10) * mm, "end": v(71.5, 10) * mm, "construction": true});
            skLineSegment(sketch, "E161.MirrorCS", {"start": v(71.4, 2.25) * mm, "end": v(71.4, 12.25) * mm, "construction": true});
            skSolve(sketch);
        }
        {
            var Q0;
            Q0 = qSketchRegion(id + "F17", true);
            extrude(context, id + "F18", {"entities" : qUnion([Q0]), "operationType" : NewBodyOperationType.ADD, "depth" : 6 * mm});
        }
        {
            var Q0;
            Q0=makeQuery(id+"F16.boolean.opBoolean","COPY",EDGE,{"derivedFrom":makeQuery(id+"F16.opExtrude","SWEPT_EDGE",EDGE,{"disambiguationData":[OSD([sQuery(id+"F0.wireOp",EDGE,"E0.bottom"),sQuery(id+"F15.wireOp",EDGE,"E100.left")])]})});
            var Q1;
            Q1=makeQuery(id+"F16.boolean.opBoolean","COPY",EDGE,{"derivedFrom":makeQuery(id+"F16.opExtrude","SWEPT_EDGE",EDGE,{"disambiguationData":[OSD([sQuery(id+"F0.wireOp",EDGE,"E0.bottom"),sQuery(id+"F15.wireOp",EDGE,"E112.MirrorCS")])]})});
            var Q2;
            Q2=makeQuery(id+"F16.boolean.opBoolean","COPY",EDGE,{"derivedFrom":makeQuery(id+"F16.opExtrude","SWEPT_EDGE",EDGE,{"disambiguationData":[OSD([sQuery(id+"F0.wireOp",EDGE,"E0.top"),sQuery(id+"F15.wireOp",EDGE,"E104.right")])]})});
            chamfer(context, id + "F19", {"entities" : qUnion([Q0, Q1, Q2]), "chamferType" : ChamferType.TWO_OFFSETS, "width1" : 1 * mm, "oppositeDirection" : false, "width2" : 2.5 * mm, "tangentPropagation" : true});
        }
        {
            var Q0;
            Q0=makeQuery(id+"F16.boolean.opBoolean","COPY",EDGE,{"derivedFrom":makeQuery(id+"F16.opExtrude","SWEPT_EDGE",EDGE,{"disambiguationData":[OSD([sQuery(id+"F0.wireOp",EDGE,"E0.top"),sQuery(id+"F15.wireOp",EDGE,"E104.left")])]})});
            var Q1;
            Q1=makeQuery(id+"F16.boolean.opBoolean","COPY",EDGE,{"derivedFrom":makeQuery(id+"F16.opExtrude","SWEPT_EDGE",EDGE,{"disambiguationData":[OSD([sQuery(id+"F0.wireOp",EDGE,"E0.bottom"),sQuery(id+"F15.wireOp",EDGE,"E111.MirrorCS")])]})});
            var Q2;
            Q2=makeQuery(id+"F16.boolean.opBoolean","COPY",EDGE,{"derivedFrom":makeQuery(id+"F16.opExtrude","SWEPT_EDGE",EDGE,{"disambiguationData":[OSD([sQuery(id+"F0.wireOp",EDGE,"E0.bottom"),sQuery(id+"F15.wireOp",EDGE,"E100.right")])]})});
            chamfer(context, id + "F20", {"entities" : qUnion([Q0, Q1, Q2]), "chamferType" : ChamferType.TWO_OFFSETS, "width1" : 2.5 * mm, "oppositeDirection" : false, "width2" : 1 * mm, "tangentPropagation" : true});
        }
        {
            var Q0;
            Q0=makeQuery(id+"F16.boolean.opBoolean","INTERSECT",EDGE,{"derivedFrom":[makeQuery(id+"F1.opExtrude","CAP_FACE",FACE,{"disambiguationData":[OSD([sQuery(id+"F0.wireOp",EDGE,"E0.bottom"),sQuery(id+"F0.wireOp",EDGE,"E0.top"),sQuery(id+"F0.wireOp",EDGE,"E0.left"),sQuery(id+"F0.wireOp",EDGE,"E0.right")])],"isStart":true}),makeQuery(id+"F16.opExtrude","SWEPT_FACE",FACE,{"disambiguationData":[OSD([sQuery(id+"F15.wireOp",EDGE,"E111.MirrorCS")])]})]});
            var Q1;
            Q1=makeQuery(id+"F16.boolean.opBoolean","INTERSECT",EDGE,{"derivedFrom":[makeQuery(id+"F1.opExtrude","CAP_FACE",FACE,{"disambiguationData":[OSD([sQuery(id+"F0.wireOp",EDGE,"E0.bottom"),sQuery(id+"F0.wireOp",EDGE,"E0.top"),sQuery(id+"F0.wireOp",EDGE,"E0.left"),sQuery(id+"F0.wireOp",EDGE,"E0.right")])],"isStart":true}),makeQuery(id+"F16.opExtrude","SWEPT_FACE",FACE,{"disambiguationData":[OSD([sQuery(id+"F15.wireOp",EDGE,"E109.MirrorCS")])]})]});
            var Q2;
            Q2=makeQuery(id+"F16.boolean.opBoolean","INTERSECT",EDGE,{"derivedFrom":[makeQuery(id+"F1.opExtrude","CAP_FACE",FACE,{"disambiguationData":[OSD([sQuery(id+"F0.wireOp",EDGE,"E0.bottom"),sQuery(id+"F0.wireOp",EDGE,"E0.top"),sQuery(id+"F0.wireOp",EDGE,"E0.left"),sQuery(id+"F0.wireOp",EDGE,"E0.right")])],"isStart":true}),makeQuery(id+"F16.opExtrude","SWEPT_FACE",FACE,{"disambiguationData":[OSD([sQuery(id+"F15.wireOp",EDGE,"E112.MirrorCS")])]})]});
            var Q3;
            Q3=makeQuery(id+"F16.boolean.opBoolean","INTERSECT",EDGE,{"derivedFrom":[makeQuery(id+"F1.opExtrude","CAP_FACE",FACE,{"disambiguationData":[OSD([sQuery(id+"F0.wireOp",EDGE,"E0.bottom"),sQuery(id+"F0.wireOp",EDGE,"E0.top"),sQuery(id+"F0.wireOp",EDGE,"E0.left"),sQuery(id+"F0.wireOp",EDGE,"E0.right")])],"isStart":true}),makeQuery(id+"F16.opExtrude","SWEPT_FACE",FACE,{"disambiguationData":[OSD([sQuery(id+"F15.wireOp",EDGE,"E100.right")])]})]});
            var Q4;
            Q4=makeQuery(id+"F16.boolean.opBoolean","INTERSECT",EDGE,{"derivedFrom":[makeQuery(id+"F1.opExtrude","CAP_FACE",FACE,{"disambiguationData":[OSD([sQuery(id+"F0.wireOp",EDGE,"E0.bottom"),sQuery(id+"F0.wireOp",EDGE,"E0.top"),sQuery(id+"F0.wireOp",EDGE,"E0.left"),sQuery(id+"F0.wireOp",EDGE,"E0.right")])],"isStart":true}),makeQuery(id+"F16.opExtrude","SWEPT_FACE",FACE,{"disambiguationData":[OSD([sQuery(id+"F15.wireOp",EDGE,"E100.bottom")])]})]});
            var Q5;
            Q5=makeQuery(id+"F16.boolean.opBoolean","INTERSECT",EDGE,{"derivedFrom":[makeQuery(id+"F1.opExtrude","CAP_FACE",FACE,{"disambiguationData":[OSD([sQuery(id+"F0.wireOp",EDGE,"E0.bottom"),sQuery(id+"F0.wireOp",EDGE,"E0.top"),sQuery(id+"F0.wireOp",EDGE,"E0.left"),sQuery(id+"F0.wireOp",EDGE,"E0.right")])],"isStart":true}),makeQuery(id+"F16.opExtrude","SWEPT_FACE",FACE,{"disambiguationData":[OSD([sQuery(id+"F15.wireOp",EDGE,"E100.left")])]})]});
            var Q6;
            Q6=makeQuery(id+"F16.boolean.opBoolean","INTERSECT",EDGE,{"derivedFrom":[makeQuery(id+"F1.opExtrude","CAP_FACE",FACE,{"disambiguationData":[OSD([sQuery(id+"F0.wireOp",EDGE,"E0.bottom"),sQuery(id+"F0.wireOp",EDGE,"E0.top"),sQuery(id+"F0.wireOp",EDGE,"E0.left"),sQuery(id+"F0.wireOp",EDGE,"E0.right")])],"isStart":true}),makeQuery(id+"F16.opExtrude","SWEPT_FACE",FACE,{"disambiguationData":[OSD([sQuery(id+"F15.wireOp",EDGE,"E108.MirrorCS")])]})]});
            var Q7;
            Q7=makeQuery(id+"F16.boolean.opBoolean","INTERSECT",EDGE,{"derivedFrom":[makeQuery(id+"F1.opExtrude","CAP_FACE",FACE,{"disambiguationData":[OSD([sQuery(id+"F0.wireOp",EDGE,"E0.bottom"),sQuery(id+"F0.wireOp",EDGE,"E0.top"),sQuery(id+"F0.wireOp",EDGE,"E0.left"),sQuery(id+"F0.wireOp",EDGE,"E0.right")])],"isStart":true}),makeQuery(id+"F16.opExtrude","SWEPT_FACE",FACE,{"disambiguationData":[OSD([sQuery(id+"F15.wireOp",EDGE,"E105.MirrorCS")])]})]});
            var Q8;
            Q8=makeQuery(id+"F16.boolean.opBoolean","INTERSECT",EDGE,{"derivedFrom":[makeQuery(id+"F1.opExtrude","CAP_FACE",FACE,{"disambiguationData":[OSD([sQuery(id+"F0.wireOp",EDGE,"E0.bottom"),sQuery(id+"F0.wireOp",EDGE,"E0.top"),sQuery(id+"F0.wireOp",EDGE,"E0.left"),sQuery(id+"F0.wireOp",EDGE,"E0.right")])],"isStart":true}),makeQuery(id+"F16.opExtrude","SWEPT_FACE",FACE,{"disambiguationData":[OSD([sQuery(id+"F15.wireOp",EDGE,"E106.MirrorCS")])]})]});
            var Q9;
            Q9=makeQuery(id+"F16.boolean.opBoolean","INTERSECT",EDGE,{"derivedFrom":[makeQuery(id+"F1.opExtrude","CAP_FACE",FACE,{"disambiguationData":[OSD([sQuery(id+"F0.wireOp",EDGE,"E0.bottom"),sQuery(id+"F0.wireOp",EDGE,"E0.top"),sQuery(id+"F0.wireOp",EDGE,"E0.left"),sQuery(id+"F0.wireOp",EDGE,"E0.right")])],"isStart":true}),makeQuery(id+"F16.opExtrude","SWEPT_FACE",FACE,{"disambiguationData":[OSD([sQuery(id+"F15.wireOp",EDGE,"E107.MirrorCS")])]})]});
            var Q10;
            Q10=makeQuery(id+"F16.boolean.opBoolean","INTERSECT",EDGE,{"derivedFrom":[makeQuery(id+"F1.opExtrude","CAP_FACE",FACE,{"disambiguationData":[OSD([sQuery(id+"F0.wireOp",EDGE,"E0.bottom"),sQuery(id+"F0.wireOp",EDGE,"E0.top"),sQuery(id+"F0.wireOp",EDGE,"E0.left"),sQuery(id+"F0.wireOp",EDGE,"E0.right")])],"isStart":true}),makeQuery(id+"F16.opExtrude","SWEPT_FACE",FACE,{"disambiguationData":[OSD([sQuery(id+"F15.wireOp",EDGE,"E104.right")])]})]});
            var Q11;
            Q11=makeQuery(id+"F16.boolean.opBoolean","INTERSECT",EDGE,{"derivedFrom":[makeQuery(id+"F1.opExtrude","CAP_FACE",FACE,{"disambiguationData":[OSD([sQuery(id+"F0.wireOp",EDGE,"E0.bottom"),sQuery(id+"F0.wireOp",EDGE,"E0.top"),sQuery(id+"F0.wireOp",EDGE,"E0.left"),sQuery(id+"F0.wireOp",EDGE,"E0.right")])],"isStart":true}),makeQuery(id+"F16.opExtrude","SWEPT_FACE",FACE,{"disambiguationData":[OSD([sQuery(id+"F15.wireOp",EDGE,"E104.left")])]})]});
            var Q12;
            Q12=makeQuery(id+"F16.boolean.opBoolean","INTERSECT",EDGE,{"derivedFrom":[makeQuery(id+"F1.opExtrude","CAP_FACE",FACE,{"disambiguationData":[OSD([sQuery(id+"F0.wireOp",EDGE,"E0.bottom"),sQuery(id+"F0.wireOp",EDGE,"E0.top"),sQuery(id+"F0.wireOp",EDGE,"E0.left"),sQuery(id+"F0.wireOp",EDGE,"E0.right")])],"isStart":true}),makeQuery(id+"F16.opExtrude","SWEPT_FACE",FACE,{"disambiguationData":[OSD([sQuery(id+"F15.wireOp",EDGE,"E104.top")])]})]});
            var Q13;
            Q13=makeQuery(id+"F16.boolean.opBoolean","INTERSECT",EDGE,{"derivedFrom":[makeQuery(id+"F1.opExtrude","CAP_FACE",FACE,{"disambiguationData":[OSD([sQuery(id+"F0.wireOp",EDGE,"E0.bottom"),sQuery(id+"F0.wireOp",EDGE,"E0.top"),sQuery(id+"F0.wireOp",EDGE,"E0.left"),sQuery(id+"F0.wireOp",EDGE,"E0.right")])],"isStart":true}),makeQuery(id+"F16.opExtrude","SWEPT_FACE",FACE,{"disambiguationData":[OSD([sQuery(id+"F15.wireOp",EDGE,"E102.left")])]})]});
            var Q14;
            Q14=makeQuery(id+"F16.boolean.opBoolean","INTERSECT",EDGE,{"derivedFrom":[makeQuery(id+"F1.opExtrude","CAP_FACE",FACE,{"disambiguationData":[OSD([sQuery(id+"F0.wireOp",EDGE,"E0.bottom"),sQuery(id+"F0.wireOp",EDGE,"E0.top"),sQuery(id+"F0.wireOp",EDGE,"E0.left"),sQuery(id+"F0.wireOp",EDGE,"E0.right")])],"isStart":true}),makeQuery(id+"F16.opExtrude","SWEPT_FACE",FACE,{"disambiguationData":[OSD([sQuery(id+"F15.wireOp",EDGE,"E102.bottom")])]})]});
            var Q15;
            Q15=makeQuery(id+"F16.boolean.opBoolean","INTERSECT",EDGE,{"derivedFrom":[makeQuery(id+"F1.opExtrude","CAP_FACE",FACE,{"disambiguationData":[OSD([sQuery(id+"F0.wireOp",EDGE,"E0.bottom"),sQuery(id+"F0.wireOp",EDGE,"E0.top"),sQuery(id+"F0.wireOp",EDGE,"E0.left"),sQuery(id+"F0.wireOp",EDGE,"E0.right")])],"isStart":true}),makeQuery(id+"F16.opExtrude","SWEPT_FACE",FACE,{"disambiguationData":[OSD([sQuery(id+"F15.wireOp",EDGE,"E102.right")])]})]});
            var Q16;
            Q16=makeQuery(id+"F16.boolean.opBoolean","INTERSECT",EDGE,{"derivedFrom":[makeQuery(id+"F1.opExtrude","CAP_FACE",FACE,{"disambiguationData":[OSD([sQuery(id+"F0.wireOp",EDGE,"E0.bottom"),sQuery(id+"F0.wireOp",EDGE,"E0.top"),sQuery(id+"F0.wireOp",EDGE,"E0.left"),sQuery(id+"F0.wireOp",EDGE,"E0.right")])],"isStart":true}),makeQuery(id+"F16.opExtrude","SWEPT_FACE",FACE,{"disambiguationData":[OSD([sQuery(id+"F15.wireOp",EDGE,"E102.top")])]})]});
            var Q17;
            {var subQ0=sQuery(id+"F0.wireOp",EDGE,"E0.top");Q17=makeQuery(id+"F19.opChamfer","BLEND_EDGE",EDGE,{"blendedFrom":[makeQuery(id+"F16.boolean.opBoolean","COPY",EDGE,{"derivedFrom":makeQuery(id+"F16.opExtrude","SWEPT_EDGE",EDGE,{"disambiguationData":[OSD([subQ0,sQuery(id+"F15.wireOp",EDGE,"E104.right")])]})}),makeQuery(id+"F1.opExtrude","CAP_FACE",FACE,{"disambiguationData":[OSD([sQuery(id+"F0.wireOp",EDGE,"E0.bottom"),subQ0,sQuery(id+"F0.wireOp",EDGE,"E0.left"),sQuery(id+"F0.wireOp",EDGE,"E0.right")])],"isStart":true})],"blendedInto":[makeQuery(id+"F1.opExtrude","CAP_FACE",FACE,{"disambiguationData":[OSD([sQuery(id+"F0.wireOp",EDGE,"E0.bottom"),subQ0,sQuery(id+"F0.wireOp",EDGE,"E0.left"),sQuery(id+"F0.wireOp",EDGE,"E0.right")])],"isStart":true})]});}
            var Q18;
            {var subQ0=sQuery(id+"F0.wireOp",EDGE,"E0.top");Q18=makeQuery(id+"F20.opChamfer","BLEND_EDGE",EDGE,{"blendedFrom":[makeQuery(id+"F16.boolean.opBoolean","COPY",EDGE,{"derivedFrom":makeQuery(id+"F16.opExtrude","SWEPT_EDGE",EDGE,{"disambiguationData":[OSD([subQ0,sQuery(id+"F15.wireOp",EDGE,"E104.left")])]})}),makeQuery(id+"F1.opExtrude","CAP_FACE",FACE,{"disambiguationData":[OSD([sQuery(id+"F0.wireOp",EDGE,"E0.bottom"),subQ0,sQuery(id+"F0.wireOp",EDGE,"E0.left"),sQuery(id+"F0.wireOp",EDGE,"E0.right")])],"isStart":true})],"blendedInto":[makeQuery(id+"F1.opExtrude","CAP_FACE",FACE,{"disambiguationData":[OSD([sQuery(id+"F0.wireOp",EDGE,"E0.bottom"),subQ0,sQuery(id+"F0.wireOp",EDGE,"E0.left"),sQuery(id+"F0.wireOp",EDGE,"E0.right")])],"isStart":true})]});}
            var Q19;
            {var subQ0=sQuery(id+"F0.wireOp",EDGE,"E0.bottom");Q19=makeQuery(id+"F20.opChamfer","BLEND_EDGE",EDGE,{"blendedFrom":[makeQuery(id+"F16.boolean.opBoolean","COPY",EDGE,{"derivedFrom":makeQuery(id+"F16.opExtrude","SWEPT_EDGE",EDGE,{"disambiguationData":[OSD([subQ0,sQuery(id+"F15.wireOp",EDGE,"E111.MirrorCS")])]})}),makeQuery(id+"F1.opExtrude","CAP_FACE",FACE,{"disambiguationData":[OSD([subQ0,sQuery(id+"F0.wireOp",EDGE,"E0.top"),sQuery(id+"F0.wireOp",EDGE,"E0.left"),sQuery(id+"F0.wireOp",EDGE,"E0.right")])],"isStart":true})],"blendedInto":[makeQuery(id+"F1.opExtrude","CAP_FACE",FACE,{"disambiguationData":[OSD([subQ0,sQuery(id+"F0.wireOp",EDGE,"E0.top"),sQuery(id+"F0.wireOp",EDGE,"E0.left"),sQuery(id+"F0.wireOp",EDGE,"E0.right")])],"isStart":true})]});}
            var Q20;
            {var subQ0=sQuery(id+"F0.wireOp",EDGE,"E0.bottom");Q20=makeQuery(id+"F19.opChamfer","BLEND_EDGE",EDGE,{"blendedFrom":[makeQuery(id+"F16.boolean.opBoolean","COPY",EDGE,{"derivedFrom":makeQuery(id+"F16.opExtrude","SWEPT_EDGE",EDGE,{"disambiguationData":[OSD([subQ0,sQuery(id+"F15.wireOp",EDGE,"E112.MirrorCS")])]})}),makeQuery(id+"F1.opExtrude","CAP_FACE",FACE,{"disambiguationData":[OSD([subQ0,sQuery(id+"F0.wireOp",EDGE,"E0.top"),sQuery(id+"F0.wireOp",EDGE,"E0.left"),sQuery(id+"F0.wireOp",EDGE,"E0.right")])],"isStart":true})],"blendedInto":[makeQuery(id+"F1.opExtrude","CAP_FACE",FACE,{"disambiguationData":[OSD([subQ0,sQuery(id+"F0.wireOp",EDGE,"E0.top"),sQuery(id+"F0.wireOp",EDGE,"E0.left"),sQuery(id+"F0.wireOp",EDGE,"E0.right")])],"isStart":true})]});}
            var Q21;
            {var subQ0=sQuery(id+"F0.wireOp",EDGE,"E0.bottom");Q21=makeQuery(id+"F20.opChamfer","BLEND_EDGE",EDGE,{"blendedFrom":[makeQuery(id+"F16.boolean.opBoolean","COPY",EDGE,{"derivedFrom":makeQuery(id+"F16.opExtrude","SWEPT_EDGE",EDGE,{"disambiguationData":[OSD([subQ0,sQuery(id+"F15.wireOp",EDGE,"E100.right")])]})}),makeQuery(id+"F1.opExtrude","CAP_FACE",FACE,{"disambiguationData":[OSD([subQ0,sQuery(id+"F0.wireOp",EDGE,"E0.top"),sQuery(id+"F0.wireOp",EDGE,"E0.left"),sQuery(id+"F0.wireOp",EDGE,"E0.right")])],"isStart":true})],"blendedInto":[makeQuery(id+"F1.opExtrude","CAP_FACE",FACE,{"disambiguationData":[OSD([subQ0,sQuery(id+"F0.wireOp",EDGE,"E0.top"),sQuery(id+"F0.wireOp",EDGE,"E0.left"),sQuery(id+"F0.wireOp",EDGE,"E0.right")])],"isStart":true})]});}
            var Q22;
            {var subQ0=sQuery(id+"F0.wireOp",EDGE,"E0.bottom");Q22=makeQuery(id+"F19.opChamfer","BLEND_EDGE",EDGE,{"blendedFrom":[makeQuery(id+"F16.boolean.opBoolean","COPY",EDGE,{"derivedFrom":makeQuery(id+"F16.opExtrude","SWEPT_EDGE",EDGE,{"disambiguationData":[OSD([subQ0,sQuery(id+"F15.wireOp",EDGE,"E100.left")])]})}),makeQuery(id+"F1.opExtrude","CAP_FACE",FACE,{"disambiguationData":[OSD([subQ0,sQuery(id+"F0.wireOp",EDGE,"E0.top"),sQuery(id+"F0.wireOp",EDGE,"E0.left"),sQuery(id+"F0.wireOp",EDGE,"E0.right")])],"isStart":true})],"blendedInto":[makeQuery(id+"F1.opExtrude","CAP_FACE",FACE,{"disambiguationData":[OSD([subQ0,sQuery(id+"F0.wireOp",EDGE,"E0.top"),sQuery(id+"F0.wireOp",EDGE,"E0.left"),sQuery(id+"F0.wireOp",EDGE,"E0.right")])],"isStart":true})]});}
            chamfer(context, id + "F21", {"entities" : qUnion([Q0, Q1, Q2, Q3, Q4, Q5, Q6, Q7, Q8, Q9, Q10, Q11, Q12, Q13, Q14, Q15, Q16, Q17, Q18, Q19, Q20, Q21, Q22]), "width" : 1.5 * mm, "tangentPropagation" : true});
        }
        {
            var Q0;
            Q0=makeQuery(id+"F4.boolean.opBoolean","MERGE",EDGE,{"derivedFrom":[makeQuery(id+"F1.opExtrude","SWEPT_EDGE",EDGE,{"disambiguationData":[OSD([sQuery(id+"F0.wireOp",EDGE,"E0.bottom"),sQuery(id+"F0.wireOp",EDGE,"E0.right")])]}),makeQuery(id+"F4.opExtrude","SWEPT_EDGE",EDGE,{"disambiguationData":[OSD([sQuery(id+"F3.wireOp",EDGE,"E14.0"),sQuery(id+"F3.wireOp",EDGE,"E15.0")])]})]});
            var Q1;
            Q1=makeQuery(id+"F4.boolean.opBoolean","MERGE",EDGE,{"derivedFrom":[makeQuery(id+"F1.opExtrude","SWEPT_EDGE",EDGE,{"disambiguationData":[OSD([sQuery(id+"F0.wireOp",EDGE,"E0.top"),sQuery(id+"F0.wireOp",EDGE,"E0.right")])]}),makeQuery(id+"F4.opExtrude","SWEPT_EDGE",EDGE,{"disambiguationData":[OSD([sQuery(id+"F3.wireOp",EDGE,"E15.0"),sQuery(id+"F3.wireOp",EDGE,"E16.0")])]})]});
            var Q2;
            Q2=makeQuery(id+"F4.boolean.opBoolean","MERGE",EDGE,{"derivedFrom":[makeQuery(id+"F1.opExtrude","SWEPT_EDGE",EDGE,{"disambiguationData":[OSD([sQuery(id+"F0.wireOp",EDGE,"E0.top"),sQuery(id+"F0.wireOp",EDGE,"E0.left")])]}),makeQuery(id+"F4.opExtrude","SWEPT_EDGE",EDGE,{"disambiguationData":[OSD([sQuery(id+"F3.wireOp",EDGE,"E13.0"),sQuery(id+"F3.wireOp",EDGE,"E16.0")])]})]});
            var Q3;
            Q3=makeQuery(id+"F4.boolean.opBoolean","MERGE",EDGE,{"derivedFrom":[makeQuery(id+"F1.opExtrude","SWEPT_EDGE",EDGE,{"disambiguationData":[OSD([sQuery(id+"F0.wireOp",EDGE,"E0.bottom"),sQuery(id+"F0.wireOp",EDGE,"E0.left")])]}),makeQuery(id+"F4.opExtrude","SWEPT_EDGE",EDGE,{"disambiguationData":[OSD([sQuery(id+"F3.wireOp",EDGE,"E13.0"),sQuery(id+"F3.wireOp",EDGE,"E14.0")])]})]});
            var Q4;
            {var subQ0=sQuery(id+"F3.wireOp",EDGE,"E16.0");var subQ2=sQuery(id+"F0.wireOp",EDGE,"E0.right");var subQ3=sQuery(id+"F15.wireOp",EDGE,"E104.right");var subQ4=sQuery(id+"F0.wireOp",EDGE,"E0.top");Q4=makeQuery(id+"F19.opChamfer","BLEND_EDGE",EDGE,{"blendedFrom":[makeQuery(id+"F16.boolean.opBoolean","COPY",EDGE,{"derivedFrom":makeQuery(id+"F16.opExtrude","SWEPT_EDGE",EDGE,{"disambiguationData":[OSD([subQ4,subQ3])]})}),makeQuery(id+"F16.boolean.opBoolean","SPLIT",FACE,{"disambiguationData":[TD([makeQuery(id+"F1.opExtrude","SWEPT_FACE",FACE,{"disambiguationData":[OSD([subQ2])]})])],"derivedFrom":makeQuery(id+"F4.boolean.opBoolean","MERGE",FACE,{"derivedFrom":[makeQuery(id+"F1.opExtrude","SWEPT_FACE",FACE,{"disambiguationData":[OSD([subQ4])]}),makeQuery(id+"F4.opExtrude","SWEPT_FACE",FACE,{"disambiguationData":[OSD([subQ0])]})]})})],"blendedInto":[makeQuery(id+"F16.boolean.opBoolean","SPLIT",FACE,{"disambiguationData":[TD([makeQuery(id+"F1.opExtrude","SWEPT_FACE",FACE,{"disambiguationData":[OSD([subQ2])]})])],"derivedFrom":makeQuery(id+"F4.boolean.opBoolean","MERGE",FACE,{"derivedFrom":[makeQuery(id+"F1.opExtrude","SWEPT_FACE",FACE,{"disambiguationData":[OSD([subQ4])]}),makeQuery(id+"F4.opExtrude","SWEPT_FACE",FACE,{"disambiguationData":[OSD([subQ0])]})]})})]});}
            var Q5;
            {var subQ0=sQuery(id+"F3.wireOp",EDGE,"E16.0");var subQ2=sQuery(id+"F0.wireOp",EDGE,"E0.left");var subQ3=sQuery(id+"F15.wireOp",EDGE,"E104.left");var subQ4=sQuery(id+"F0.wireOp",EDGE,"E0.top");Q5=makeQuery(id+"F20.opChamfer","BLEND_EDGE",EDGE,{"blendedFrom":[makeQuery(id+"F16.boolean.opBoolean","COPY",EDGE,{"derivedFrom":makeQuery(id+"F16.opExtrude","SWEPT_EDGE",EDGE,{"disambiguationData":[OSD([subQ4,subQ3])]})}),makeQuery(id+"F16.boolean.opBoolean","SPLIT",FACE,{"disambiguationData":[TD([makeQuery(id+"F1.opExtrude","SWEPT_FACE",FACE,{"disambiguationData":[OSD([subQ2])]})])],"derivedFrom":makeQuery(id+"F4.boolean.opBoolean","MERGE",FACE,{"derivedFrom":[makeQuery(id+"F1.opExtrude","SWEPT_FACE",FACE,{"disambiguationData":[OSD([subQ4])]}),makeQuery(id+"F4.opExtrude","SWEPT_FACE",FACE,{"disambiguationData":[OSD([subQ0])]})]})})],"blendedInto":[makeQuery(id+"F16.boolean.opBoolean","SPLIT",FACE,{"disambiguationData":[TD([makeQuery(id+"F1.opExtrude","SWEPT_FACE",FACE,{"disambiguationData":[OSD([subQ2])]})])],"derivedFrom":makeQuery(id+"F4.boolean.opBoolean","MERGE",FACE,{"derivedFrom":[makeQuery(id+"F1.opExtrude","SWEPT_FACE",FACE,{"disambiguationData":[OSD([subQ4])]}),makeQuery(id+"F4.opExtrude","SWEPT_FACE",FACE,{"disambiguationData":[OSD([subQ0])]})]})})]});}
            var Q6;
            {var subQ0=sQuery(id+"F3.wireOp",EDGE,"E16.0");var subQ2=sQuery(id+"F0.wireOp",EDGE,"E0.right");var subQ3=sQuery(id+"F15.wireOp",EDGE,"E104.right");var subQ4=sQuery(id+"F0.wireOp",EDGE,"E0.top");var subQ5=makeQuery(id+"F1.opExtrude","CAP_FACE",FACE,{"disambiguationData":[OSD([sQuery(id+"F0.wireOp",EDGE,"E0.bottom"),subQ4,sQuery(id+"F0.wireOp",EDGE,"E0.left"),subQ2])],"isStart":true});Q6=makeQuery(id+"F21.opChamfer","BLEND_EDGE",EDGE,{"blendedFrom":[makeQuery(id+"F19.opChamfer","BLEND_EDGE",EDGE,{"blendedFrom":[makeQuery(id+"F16.boolean.opBoolean","COPY",EDGE,{"derivedFrom":makeQuery(id+"F16.opExtrude","SWEPT_EDGE",EDGE,{"disambiguationData":[OSD([subQ4,subQ3])]})}),subQ5],"blendedInto":[subQ5]}),makeQuery(id+"F16.boolean.opBoolean","SPLIT",FACE,{"disambiguationData":[TD([makeQuery(id+"F1.opExtrude","SWEPT_FACE",FACE,{"disambiguationData":[OSD([subQ2])]})])],"derivedFrom":makeQuery(id+"F4.boolean.opBoolean","MERGE",FACE,{"derivedFrom":[makeQuery(id+"F1.opExtrude","SWEPT_FACE",FACE,{"disambiguationData":[OSD([subQ4])]}),makeQuery(id+"F4.opExtrude","SWEPT_FACE",FACE,{"disambiguationData":[OSD([subQ0])]})]})})],"blendedInto":[makeQuery(id+"F16.boolean.opBoolean","SPLIT",FACE,{"disambiguationData":[TD([makeQuery(id+"F1.opExtrude","SWEPT_FACE",FACE,{"disambiguationData":[OSD([subQ2])]})])],"derivedFrom":makeQuery(id+"F4.boolean.opBoolean","MERGE",FACE,{"derivedFrom":[makeQuery(id+"F1.opExtrude","SWEPT_FACE",FACE,{"disambiguationData":[OSD([subQ4])]}),makeQuery(id+"F4.opExtrude","SWEPT_FACE",FACE,{"disambiguationData":[OSD([subQ0])]})]})})]});}
            var Q7;
            {var subQ0=sQuery(id+"F0.wireOp",EDGE,"E0.top");var subQ1=makeQuery(id+"F1.opExtrude","CAP_FACE",FACE,{"disambiguationData":[OSD([sQuery(id+"F0.wireOp",EDGE,"E0.bottom"),subQ0,sQuery(id+"F0.wireOp",EDGE,"E0.left"),sQuery(id+"F0.wireOp",EDGE,"E0.right")])],"isStart":true});Q7=makeQuery(id+"F21.opChamfer","BLEND_EDGE",EDGE,{"blendedFrom":[makeQuery(id+"F16.boolean.opBoolean","INTERSECT",EDGE,{"derivedFrom":[subQ1,makeQuery(id+"F16.opExtrude","SWEPT_FACE",FACE,{"disambiguationData":[OSD([sQuery(id+"F15.wireOp",EDGE,"E104.top")])]})]}),makeQuery(id+"F19.opChamfer","BLEND_EDGE",EDGE,{"blendedFrom":[makeQuery(id+"F16.boolean.opBoolean","COPY",EDGE,{"derivedFrom":makeQuery(id+"F16.opExtrude","SWEPT_EDGE",EDGE,{"disambiguationData":[OSD([subQ0,sQuery(id+"F15.wireOp",EDGE,"E104.right")])]})}),subQ1],"blendedInto":[subQ1]})],"blendedInto":[]});}
            var Q8;
            {var subQ0=sQuery(id+"F0.wireOp",EDGE,"E0.top");var subQ1=makeQuery(id+"F1.opExtrude","CAP_FACE",FACE,{"disambiguationData":[OSD([sQuery(id+"F0.wireOp",EDGE,"E0.bottom"),subQ0,sQuery(id+"F0.wireOp",EDGE,"E0.left"),sQuery(id+"F0.wireOp",EDGE,"E0.right")])],"isStart":true});Q8=makeQuery(id+"F21.opChamfer","BLEND_EDGE",EDGE,{"blendedFrom":[makeQuery(id+"F16.boolean.opBoolean","INTERSECT",EDGE,{"derivedFrom":[subQ1,makeQuery(id+"F16.opExtrude","SWEPT_FACE",FACE,{"disambiguationData":[OSD([sQuery(id+"F15.wireOp",EDGE,"E104.top")])]})]}),makeQuery(id+"F20.opChamfer","BLEND_EDGE",EDGE,{"blendedFrom":[makeQuery(id+"F16.boolean.opBoolean","COPY",EDGE,{"derivedFrom":makeQuery(id+"F16.opExtrude","SWEPT_EDGE",EDGE,{"disambiguationData":[OSD([subQ0,sQuery(id+"F15.wireOp",EDGE,"E104.left")])]})}),subQ1],"blendedInto":[subQ1]})],"blendedInto":[]});}
            var Q9;
            {var subQ0=sQuery(id+"F3.wireOp",EDGE,"E16.0");var subQ2=sQuery(id+"F0.wireOp",EDGE,"E0.left");var subQ3=sQuery(id+"F15.wireOp",EDGE,"E104.left");var subQ4=sQuery(id+"F0.wireOp",EDGE,"E0.top");var subQ5=makeQuery(id+"F1.opExtrude","CAP_FACE",FACE,{"disambiguationData":[OSD([sQuery(id+"F0.wireOp",EDGE,"E0.bottom"),subQ4,subQ2,sQuery(id+"F0.wireOp",EDGE,"E0.right")])],"isStart":true});Q9=makeQuery(id+"F21.opChamfer","BLEND_EDGE",EDGE,{"blendedFrom":[makeQuery(id+"F20.opChamfer","BLEND_EDGE",EDGE,{"blendedFrom":[makeQuery(id+"F16.boolean.opBoolean","COPY",EDGE,{"derivedFrom":makeQuery(id+"F16.opExtrude","SWEPT_EDGE",EDGE,{"disambiguationData":[OSD([subQ4,subQ3])]})}),subQ5],"blendedInto":[subQ5]}),makeQuery(id+"F16.boolean.opBoolean","SPLIT",FACE,{"disambiguationData":[TD([makeQuery(id+"F1.opExtrude","SWEPT_FACE",FACE,{"disambiguationData":[OSD([subQ2])]})])],"derivedFrom":makeQuery(id+"F4.boolean.opBoolean","MERGE",FACE,{"derivedFrom":[makeQuery(id+"F1.opExtrude","SWEPT_FACE",FACE,{"disambiguationData":[OSD([subQ4])]}),makeQuery(id+"F4.opExtrude","SWEPT_FACE",FACE,{"disambiguationData":[OSD([subQ0])]})]})})],"blendedInto":[makeQuery(id+"F16.boolean.opBoolean","SPLIT",FACE,{"disambiguationData":[TD([makeQuery(id+"F1.opExtrude","SWEPT_FACE",FACE,{"disambiguationData":[OSD([subQ2])]})])],"derivedFrom":makeQuery(id+"F4.boolean.opBoolean","MERGE",FACE,{"derivedFrom":[makeQuery(id+"F1.opExtrude","SWEPT_FACE",FACE,{"disambiguationData":[OSD([subQ4])]}),makeQuery(id+"F4.opExtrude","SWEPT_FACE",FACE,{"disambiguationData":[OSD([subQ0])]})]})})]});}
            var Q10;
            {var subQ2=sQuery(id+"F0.wireOp",EDGE,"E0.bottom");var subQ6=sQuery(id+"F0.wireOp",EDGE,"E0.right");var subQ7=sQuery(id+"F3.wireOp",EDGE,"E14.0");var subQ9=sQuery(id+"F0.wireOp",EDGE,"E0.left");var subQ10=sQuery(id+"F0.wireOp",EDGE,"E0.top");var subQ11=makeQuery(id+"F1.opExtrude","CAP_FACE",FACE,{"disambiguationData":[OSD([subQ2,subQ10,subQ9,subQ6])],"isStart":true});var subQ12=sQuery(id+"F15.wireOp",EDGE,"E100.left");Q10=makeQuery(id+"F21.opChamfer","BLEND_EDGE",EDGE,{"blendedFrom":[makeQuery(id+"F19.opChamfer","BLEND_EDGE",EDGE,{"blendedFrom":[makeQuery(id+"F16.boolean.opBoolean","COPY",EDGE,{"derivedFrom":makeQuery(id+"F16.opExtrude","SWEPT_EDGE",EDGE,{"disambiguationData":[OSD([subQ2,subQ12])]})}),subQ11],"blendedInto":[subQ11]}),makeQuery(id+"F16.boolean.opBoolean","SPLIT",FACE,{"disambiguationData":[TD([makeQuery(id+"F1.opExtrude","SWEPT_FACE",FACE,{"disambiguationData":[OSD([subQ9])]})])],"derivedFrom":makeQuery(id+"F4.boolean.opBoolean","MERGE",FACE,{"derivedFrom":[makeQuery(id+"F1.opExtrude","SWEPT_FACE",FACE,{"disambiguationData":[OSD([subQ2])]}),makeQuery(id+"F4.opExtrude","SWEPT_FACE",FACE,{"disambiguationData":[OSD([subQ7])]})]})})],"blendedInto":[makeQuery(id+"F16.boolean.opBoolean","SPLIT",FACE,{"disambiguationData":[TD([makeQuery(id+"F1.opExtrude","SWEPT_FACE",FACE,{"disambiguationData":[OSD([subQ9])]})])],"derivedFrom":makeQuery(id+"F4.boolean.opBoolean","MERGE",FACE,{"derivedFrom":[makeQuery(id+"F1.opExtrude","SWEPT_FACE",FACE,{"disambiguationData":[OSD([subQ2])]}),makeQuery(id+"F4.opExtrude","SWEPT_FACE",FACE,{"disambiguationData":[OSD([subQ7])]})]})})]});}
            var Q11;
            {var subQ0=sQuery(id+"F0.wireOp",EDGE,"E0.bottom");var subQ1=makeQuery(id+"F1.opExtrude","CAP_FACE",FACE,{"disambiguationData":[OSD([subQ0,sQuery(id+"F0.wireOp",EDGE,"E0.top"),sQuery(id+"F0.wireOp",EDGE,"E0.left"),sQuery(id+"F0.wireOp",EDGE,"E0.right")])],"isStart":true});Q11=makeQuery(id+"F21.opChamfer","BLEND_EDGE",EDGE,{"blendedFrom":[makeQuery(id+"F19.opChamfer","BLEND_EDGE",EDGE,{"blendedFrom":[makeQuery(id+"F16.boolean.opBoolean","COPY",EDGE,{"derivedFrom":makeQuery(id+"F16.opExtrude","SWEPT_EDGE",EDGE,{"disambiguationData":[OSD([subQ0,sQuery(id+"F15.wireOp",EDGE,"E100.left")])]})}),subQ1],"blendedInto":[subQ1]}),makeQuery(id+"F16.boolean.opBoolean","INTERSECT",EDGE,{"derivedFrom":[subQ1,makeQuery(id+"F16.opExtrude","SWEPT_FACE",FACE,{"disambiguationData":[OSD([sQuery(id+"F15.wireOp",EDGE,"E100.bottom")])]})]})],"blendedInto":[]});}
            var Q12;
            {var subQ0=sQuery(id+"F0.wireOp",EDGE,"E0.bottom");var subQ1=makeQuery(id+"F1.opExtrude","CAP_FACE",FACE,{"disambiguationData":[OSD([subQ0,sQuery(id+"F0.wireOp",EDGE,"E0.top"),sQuery(id+"F0.wireOp",EDGE,"E0.left"),sQuery(id+"F0.wireOp",EDGE,"E0.right")])],"isStart":true});Q12=makeQuery(id+"F21.opChamfer","BLEND_EDGE",EDGE,{"blendedFrom":[makeQuery(id+"F20.opChamfer","BLEND_EDGE",EDGE,{"blendedFrom":[makeQuery(id+"F16.boolean.opBoolean","COPY",EDGE,{"derivedFrom":makeQuery(id+"F16.opExtrude","SWEPT_EDGE",EDGE,{"disambiguationData":[OSD([subQ0,sQuery(id+"F15.wireOp",EDGE,"E100.right")])]})}),subQ1],"blendedInto":[subQ1]}),makeQuery(id+"F16.boolean.opBoolean","INTERSECT",EDGE,{"derivedFrom":[subQ1,makeQuery(id+"F16.opExtrude","SWEPT_FACE",FACE,{"disambiguationData":[OSD([sQuery(id+"F15.wireOp",EDGE,"E100.bottom")])]})]})],"blendedInto":[]});}
            var Q13;
            {var subQ0=sQuery(id+"F15.wireOp",EDGE,"E100.right");var subQ1=sQuery(id+"F0.wireOp",EDGE,"E0.right");var subQ5=sQuery(id+"F0.wireOp",EDGE,"E0.bottom");var subQ9=sQuery(id+"F0.wireOp",EDGE,"E0.left");var subQ10=sQuery(id+"F0.wireOp",EDGE,"E0.top");var subQ11=sQuery(id+"F3.wireOp",EDGE,"E14.0");var subQ12=makeQuery(id+"F1.opExtrude","CAP_FACE",FACE,{"disambiguationData":[OSD([subQ5,subQ10,subQ9,subQ1])],"isStart":true});Q13=makeQuery(id+"F21.opChamfer","BLEND_EDGE",EDGE,{"blendedFrom":[makeQuery(id+"F20.opChamfer","BLEND_EDGE",EDGE,{"blendedFrom":[makeQuery(id+"F16.boolean.opBoolean","COPY",EDGE,{"derivedFrom":makeQuery(id+"F16.opExtrude","SWEPT_EDGE",EDGE,{"disambiguationData":[OSD([subQ5,subQ0])]})}),subQ12],"blendedInto":[subQ12]}),makeQuery(id+"F16.boolean.opBoolean","SPLIT",FACE,{"disambiguationData":[TD([makeQuery(id+"F16.opExtrude","SWEPT_FACE",FACE,{"disambiguationData":[OSD([subQ0])]})])],"derivedFrom":makeQuery(id+"F4.boolean.opBoolean","MERGE",FACE,{"derivedFrom":[makeQuery(id+"F1.opExtrude","SWEPT_FACE",FACE,{"disambiguationData":[OSD([subQ5])]}),makeQuery(id+"F4.opExtrude","SWEPT_FACE",FACE,{"disambiguationData":[OSD([subQ11])]})]})})],"blendedInto":[makeQuery(id+"F16.boolean.opBoolean","SPLIT",FACE,{"disambiguationData":[TD([makeQuery(id+"F16.opExtrude","SWEPT_FACE",FACE,{"disambiguationData":[OSD([subQ0])]})])],"derivedFrom":makeQuery(id+"F4.boolean.opBoolean","MERGE",FACE,{"derivedFrom":[makeQuery(id+"F1.opExtrude","SWEPT_FACE",FACE,{"disambiguationData":[OSD([subQ5])]}),makeQuery(id+"F4.opExtrude","SWEPT_FACE",FACE,{"disambiguationData":[OSD([subQ11])]})]})})]});}
            var Q14;
            {var subQ0=sQuery(id+"F0.wireOp",EDGE,"E0.right");var subQ4=sQuery(id+"F0.wireOp",EDGE,"E0.bottom");var subQ8=sQuery(id+"F0.wireOp",EDGE,"E0.left");var subQ9=sQuery(id+"F0.wireOp",EDGE,"E0.top");var subQ10=sQuery(id+"F3.wireOp",EDGE,"E14.0");var subQ11=makeQuery(id+"F1.opExtrude","CAP_FACE",FACE,{"disambiguationData":[OSD([subQ4,subQ9,subQ8,subQ0])],"isStart":true});var subQ12=sQuery(id+"F15.wireOp",EDGE,"E112.MirrorCS");Q14=makeQuery(id+"F21.opChamfer","BLEND_EDGE",EDGE,{"blendedFrom":[makeQuery(id+"F19.opChamfer","BLEND_EDGE",EDGE,{"blendedFrom":[makeQuery(id+"F16.boolean.opBoolean","COPY",EDGE,{"derivedFrom":makeQuery(id+"F16.opExtrude","SWEPT_EDGE",EDGE,{"disambiguationData":[OSD([subQ4,subQ12])]})}),subQ11],"blendedInto":[subQ11]}),makeQuery(id+"F16.boolean.opBoolean","SPLIT",FACE,{"disambiguationData":[TD([makeQuery(id+"F16.opExtrude","SWEPT_FACE",FACE,{"disambiguationData":[OSD([sQuery(id+"F15.wireOp",EDGE,"E100.right")])]})])],"derivedFrom":makeQuery(id+"F4.boolean.opBoolean","MERGE",FACE,{"derivedFrom":[makeQuery(id+"F1.opExtrude","SWEPT_FACE",FACE,{"disambiguationData":[OSD([subQ4])]}),makeQuery(id+"F4.opExtrude","SWEPT_FACE",FACE,{"disambiguationData":[OSD([subQ10])]})]})})],"blendedInto":[makeQuery(id+"F16.boolean.opBoolean","SPLIT",FACE,{"disambiguationData":[TD([makeQuery(id+"F16.opExtrude","SWEPT_FACE",FACE,{"disambiguationData":[OSD([sQuery(id+"F15.wireOp",EDGE,"E100.right")])]})])],"derivedFrom":makeQuery(id+"F4.boolean.opBoolean","MERGE",FACE,{"derivedFrom":[makeQuery(id+"F1.opExtrude","SWEPT_FACE",FACE,{"disambiguationData":[OSD([subQ4])]}),makeQuery(id+"F4.opExtrude","SWEPT_FACE",FACE,{"disambiguationData":[OSD([subQ10])]})]})})]});}
            var Q15;
            {var subQ0=sQuery(id+"F0.wireOp",EDGE,"E0.bottom");var subQ1=makeQuery(id+"F1.opExtrude","CAP_FACE",FACE,{"disambiguationData":[OSD([subQ0,sQuery(id+"F0.wireOp",EDGE,"E0.top"),sQuery(id+"F0.wireOp",EDGE,"E0.left"),sQuery(id+"F0.wireOp",EDGE,"E0.right")])],"isStart":true});Q15=makeQuery(id+"F21.opChamfer","BLEND_EDGE",EDGE,{"blendedFrom":[makeQuery(id+"F19.opChamfer","BLEND_EDGE",EDGE,{"blendedFrom":[makeQuery(id+"F16.boolean.opBoolean","COPY",EDGE,{"derivedFrom":makeQuery(id+"F16.opExtrude","SWEPT_EDGE",EDGE,{"disambiguationData":[OSD([subQ0,sQuery(id+"F15.wireOp",EDGE,"E112.MirrorCS")])]})}),subQ1],"blendedInto":[subQ1]}),makeQuery(id+"F16.boolean.opBoolean","INTERSECT",EDGE,{"derivedFrom":[subQ1,makeQuery(id+"F16.opExtrude","SWEPT_FACE",FACE,{"disambiguationData":[OSD([sQuery(id+"F15.wireOp",EDGE,"E109.MirrorCS")])]})]})],"blendedInto":[]});}
            var Q16;
            {var subQ0=sQuery(id+"F0.wireOp",EDGE,"E0.bottom");var subQ1=makeQuery(id+"F1.opExtrude","CAP_FACE",FACE,{"disambiguationData":[OSD([subQ0,sQuery(id+"F0.wireOp",EDGE,"E0.top"),sQuery(id+"F0.wireOp",EDGE,"E0.left"),sQuery(id+"F0.wireOp",EDGE,"E0.right")])],"isStart":true});Q16=makeQuery(id+"F21.opChamfer","BLEND_EDGE",EDGE,{"blendedFrom":[makeQuery(id+"F20.opChamfer","BLEND_EDGE",EDGE,{"blendedFrom":[makeQuery(id+"F16.boolean.opBoolean","COPY",EDGE,{"derivedFrom":makeQuery(id+"F16.opExtrude","SWEPT_EDGE",EDGE,{"disambiguationData":[OSD([subQ0,sQuery(id+"F15.wireOp",EDGE,"E111.MirrorCS")])]})}),subQ1],"blendedInto":[subQ1]}),makeQuery(id+"F16.boolean.opBoolean","INTERSECT",EDGE,{"derivedFrom":[subQ1,makeQuery(id+"F16.opExtrude","SWEPT_FACE",FACE,{"disambiguationData":[OSD([sQuery(id+"F15.wireOp",EDGE,"E109.MirrorCS")])]})]})],"blendedInto":[]});}
            var Q17;
            {var subQ2=sQuery(id+"F0.wireOp",EDGE,"E0.bottom");var subQ4=sQuery(id+"F0.wireOp",EDGE,"E0.left");var subQ5=sQuery(id+"F0.wireOp",EDGE,"E0.right");var subQ6=sQuery(id+"F0.wireOp",EDGE,"E0.top");var subQ7=makeQuery(id+"F1.opExtrude","CAP_FACE",FACE,{"disambiguationData":[OSD([subQ2,subQ6,subQ4,subQ5])],"isStart":true});var subQ8=sQuery(id+"F15.wireOp",EDGE,"E111.MirrorCS");var subQ9=sQuery(id+"F3.wireOp",EDGE,"E14.0");Q17=makeQuery(id+"F21.opChamfer","BLEND_EDGE",EDGE,{"blendedFrom":[makeQuery(id+"F20.opChamfer","BLEND_EDGE",EDGE,{"blendedFrom":[makeQuery(id+"F16.boolean.opBoolean","COPY",EDGE,{"derivedFrom":makeQuery(id+"F16.opExtrude","SWEPT_EDGE",EDGE,{"disambiguationData":[OSD([subQ2,subQ8])]})}),subQ7],"blendedInto":[subQ7]}),makeQuery(id+"F16.boolean.opBoolean","SPLIT",FACE,{"disambiguationData":[TD([makeQuery(id+"F1.opExtrude","SWEPT_FACE",FACE,{"disambiguationData":[OSD([subQ5])]})])],"derivedFrom":makeQuery(id+"F4.boolean.opBoolean","MERGE",FACE,{"derivedFrom":[makeQuery(id+"F1.opExtrude","SWEPT_FACE",FACE,{"disambiguationData":[OSD([subQ2])]}),makeQuery(id+"F4.opExtrude","SWEPT_FACE",FACE,{"disambiguationData":[OSD([subQ9])]})]})})],"blendedInto":[makeQuery(id+"F16.boolean.opBoolean","SPLIT",FACE,{"disambiguationData":[TD([makeQuery(id+"F1.opExtrude","SWEPT_FACE",FACE,{"disambiguationData":[OSD([subQ5])]})])],"derivedFrom":makeQuery(id+"F4.boolean.opBoolean","MERGE",FACE,{"derivedFrom":[makeQuery(id+"F1.opExtrude","SWEPT_FACE",FACE,{"disambiguationData":[OSD([subQ2])]}),makeQuery(id+"F4.opExtrude","SWEPT_FACE",FACE,{"disambiguationData":[OSD([subQ9])]})]})})]});}
            fillet(context, id + "F22", {"entities" : qUnion([Q0, Q1, Q2, Q3, Q4, Q5, Q6, Q7, Q8, Q9, Q10, Q11, Q12, Q13, Q14, Q15, Q16, Q17]), "radius" : 0.5 * mm, "tangentPropagation" : true, "allowEdgeOverflow" : false});
        }
        {
            var Q0;
            {var subQ0=sQuery(id+"F0.wireOp",EDGE,"E0.left");var subQ1=sQuery(id+"F0.wireOp",EDGE,"E0.bottom");Q0=makeQuery(id+"F16.boolean.opBoolean","SPLIT",EDGE,{"disambiguationData":[TD([makeQuery(id+"F1.opExtrude","SWEPT_FACE",FACE,{"disambiguationData":[OSD([subQ0])]})])],"derivedFrom":makeQuery(id+"F1.opExtrude","CAP_EDGE",EDGE,{"disambiguationData":[OSD([subQ1])],"isStart":true})});}
            fillet(context, id + "F23", {"entities" : qUnion([Q0]), "radius" : 0.5 * mm, "tangentPropagation" : true, "allowEdgeOverflow" : false});
        }
        {
            var Q0;
            {var subQ0=makeQuery(id+"F1.opExtrude","CAP_FACE",FACE,{"disambiguationData":[OSD([sQuery(id+"F0.wireOp",EDGE,"E0.bottom"),sQuery(id+"F0.wireOp",EDGE,"E0.top"),sQuery(id+"F0.wireOp",EDGE,"E0.left"),sQuery(id+"F0.wireOp",EDGE,"E0.right")])],"isStart":true});Q0=makeQuery(id+"F21.opChamfer","BLEND_EDGE",EDGE,{"blendedFrom":[makeQuery(id+"F16.boolean.opBoolean","INTERSECT",EDGE,{"derivedFrom":[subQ0,makeQuery(id+"F16.opExtrude","SWEPT_FACE",FACE,{"disambiguationData":[OSD([sQuery(id+"F15.wireOp",EDGE,"E102.top")])]})]}),subQ0],"blendedInto":[subQ0]});}
            var Q1;
            {var subQ0=makeQuery(id+"F1.opExtrude","CAP_FACE",FACE,{"disambiguationData":[OSD([sQuery(id+"F0.wireOp",EDGE,"E0.bottom"),sQuery(id+"F0.wireOp",EDGE,"E0.top"),sQuery(id+"F0.wireOp",EDGE,"E0.left"),sQuery(id+"F0.wireOp",EDGE,"E0.right")])],"isStart":true});Q1=makeQuery(id+"F21.opChamfer","BLEND_EDGE",EDGE,{"blendedFrom":[makeQuery(id+"F16.boolean.opBoolean","INTERSECT",EDGE,{"derivedFrom":[subQ0,makeQuery(id+"F16.opExtrude","SWEPT_FACE",FACE,{"disambiguationData":[OSD([sQuery(id+"F15.wireOp",EDGE,"E102.top")])]})]}),makeQuery(id+"F16.boolean.opBoolean","INTERSECT",EDGE,{"derivedFrom":[subQ0,makeQuery(id+"F16.opExtrude","SWEPT_FACE",FACE,{"disambiguationData":[OSD([sQuery(id+"F15.wireOp",EDGE,"E102.right")])]})]})],"blendedInto":[]});}
            var Q2;
            {var subQ0=makeQuery(id+"F1.opExtrude","CAP_FACE",FACE,{"disambiguationData":[OSD([sQuery(id+"F0.wireOp",EDGE,"E0.bottom"),sQuery(id+"F0.wireOp",EDGE,"E0.top"),sQuery(id+"F0.wireOp",EDGE,"E0.left"),sQuery(id+"F0.wireOp",EDGE,"E0.right")])],"isStart":true});Q2=makeQuery(id+"F21.opChamfer","BLEND_EDGE",EDGE,{"blendedFrom":[makeQuery(id+"F16.boolean.opBoolean","INTERSECT",EDGE,{"derivedFrom":[subQ0,makeQuery(id+"F16.opExtrude","SWEPT_FACE",FACE,{"disambiguationData":[OSD([sQuery(id+"F15.wireOp",EDGE,"E102.bottom")])]})]}),makeQuery(id+"F16.boolean.opBoolean","INTERSECT",EDGE,{"derivedFrom":[subQ0,makeQuery(id+"F16.opExtrude","SWEPT_FACE",FACE,{"disambiguationData":[OSD([sQuery(id+"F15.wireOp",EDGE,"E102.right")])]})]})],"blendedInto":[]});}
            var Q3;
            {var subQ0=makeQuery(id+"F1.opExtrude","CAP_FACE",FACE,{"disambiguationData":[OSD([sQuery(id+"F0.wireOp",EDGE,"E0.bottom"),sQuery(id+"F0.wireOp",EDGE,"E0.top"),sQuery(id+"F0.wireOp",EDGE,"E0.left"),sQuery(id+"F0.wireOp",EDGE,"E0.right")])],"isStart":true});Q3=makeQuery(id+"F21.opChamfer","BLEND_EDGE",EDGE,{"blendedFrom":[makeQuery(id+"F16.boolean.opBoolean","INTERSECT",EDGE,{"derivedFrom":[subQ0,makeQuery(id+"F16.opExtrude","SWEPT_FACE",FACE,{"disambiguationData":[OSD([sQuery(id+"F15.wireOp",EDGE,"E102.bottom")])]})]}),makeQuery(id+"F16.boolean.opBoolean","INTERSECT",EDGE,{"derivedFrom":[subQ0,makeQuery(id+"F16.opExtrude","SWEPT_FACE",FACE,{"disambiguationData":[OSD([sQuery(id+"F15.wireOp",EDGE,"E102.left")])]})]})],"blendedInto":[]});}
            var Q4;
            {var subQ0=makeQuery(id+"F1.opExtrude","CAP_FACE",FACE,{"disambiguationData":[OSD([sQuery(id+"F0.wireOp",EDGE,"E0.bottom"),sQuery(id+"F0.wireOp",EDGE,"E0.top"),sQuery(id+"F0.wireOp",EDGE,"E0.left"),sQuery(id+"F0.wireOp",EDGE,"E0.right")])],"isStart":true});Q4=makeQuery(id+"F21.opChamfer","BLEND_EDGE",EDGE,{"blendedFrom":[makeQuery(id+"F16.boolean.opBoolean","INTERSECT",EDGE,{"derivedFrom":[subQ0,makeQuery(id+"F16.opExtrude","SWEPT_FACE",FACE,{"disambiguationData":[OSD([sQuery(id+"F15.wireOp",EDGE,"E102.top")])]})]}),makeQuery(id+"F16.boolean.opBoolean","INTERSECT",EDGE,{"derivedFrom":[subQ0,makeQuery(id+"F16.opExtrude","SWEPT_FACE",FACE,{"disambiguationData":[OSD([sQuery(id+"F15.wireOp",EDGE,"E102.left")])]})]})],"blendedInto":[]});}
            var Q5;
            {var subQ0=makeQuery(id+"F1.opExtrude","CAP_FACE",FACE,{"disambiguationData":[OSD([sQuery(id+"F0.wireOp",EDGE,"E0.bottom"),sQuery(id+"F0.wireOp",EDGE,"E0.top"),sQuery(id+"F0.wireOp",EDGE,"E0.left"),sQuery(id+"F0.wireOp",EDGE,"E0.right")])],"isStart":true});Q5=makeQuery(id+"F21.opChamfer","BLEND_EDGE",EDGE,{"blendedFrom":[makeQuery(id+"F16.boolean.opBoolean","INTERSECT",EDGE,{"derivedFrom":[subQ0,makeQuery(id+"F16.opExtrude","SWEPT_FACE",FACE,{"disambiguationData":[OSD([sQuery(id+"F15.wireOp",EDGE,"E105.MirrorCS")])]})]}),makeQuery(id+"F16.boolean.opBoolean","INTERSECT",EDGE,{"derivedFrom":[subQ0,makeQuery(id+"F16.opExtrude","SWEPT_FACE",FACE,{"disambiguationData":[OSD([sQuery(id+"F15.wireOp",EDGE,"E106.MirrorCS")])]})]})],"blendedInto":[]});}
            var Q6;
            {var subQ0=makeQuery(id+"F1.opExtrude","CAP_FACE",FACE,{"disambiguationData":[OSD([sQuery(id+"F0.wireOp",EDGE,"E0.bottom"),sQuery(id+"F0.wireOp",EDGE,"E0.top"),sQuery(id+"F0.wireOp",EDGE,"E0.left"),sQuery(id+"F0.wireOp",EDGE,"E0.right")])],"isStart":true});Q6=makeQuery(id+"F21.opChamfer","BLEND_EDGE",EDGE,{"blendedFrom":[makeQuery(id+"F16.boolean.opBoolean","INTERSECT",EDGE,{"derivedFrom":[subQ0,makeQuery(id+"F16.opExtrude","SWEPT_FACE",FACE,{"disambiguationData":[OSD([sQuery(id+"F15.wireOp",EDGE,"E106.MirrorCS")])]})]}),makeQuery(id+"F16.boolean.opBoolean","INTERSECT",EDGE,{"derivedFrom":[subQ0,makeQuery(id+"F16.opExtrude","SWEPT_FACE",FACE,{"disambiguationData":[OSD([sQuery(id+"F15.wireOp",EDGE,"E107.MirrorCS")])]})]})],"blendedInto":[]});}
            var Q7;
            {var subQ0=makeQuery(id+"F1.opExtrude","CAP_FACE",FACE,{"disambiguationData":[OSD([sQuery(id+"F0.wireOp",EDGE,"E0.bottom"),sQuery(id+"F0.wireOp",EDGE,"E0.top"),sQuery(id+"F0.wireOp",EDGE,"E0.left"),sQuery(id+"F0.wireOp",EDGE,"E0.right")])],"isStart":true});Q7=makeQuery(id+"F21.opChamfer","BLEND_EDGE",EDGE,{"blendedFrom":[makeQuery(id+"F16.boolean.opBoolean","INTERSECT",EDGE,{"derivedFrom":[subQ0,makeQuery(id+"F16.opExtrude","SWEPT_FACE",FACE,{"disambiguationData":[OSD([sQuery(id+"F15.wireOp",EDGE,"E107.MirrorCS")])]})]}),makeQuery(id+"F16.boolean.opBoolean","INTERSECT",EDGE,{"derivedFrom":[subQ0,makeQuery(id+"F16.opExtrude","SWEPT_FACE",FACE,{"disambiguationData":[OSD([sQuery(id+"F15.wireOp",EDGE,"E108.MirrorCS")])]})]})],"blendedInto":[]});}
            var Q8;
            {var subQ0=makeQuery(id+"F1.opExtrude","CAP_FACE",FACE,{"disambiguationData":[OSD([sQuery(id+"F0.wireOp",EDGE,"E0.bottom"),sQuery(id+"F0.wireOp",EDGE,"E0.top"),sQuery(id+"F0.wireOp",EDGE,"E0.left"),sQuery(id+"F0.wireOp",EDGE,"E0.right")])],"isStart":true});Q8=makeQuery(id+"F21.opChamfer","BLEND_EDGE",EDGE,{"blendedFrom":[makeQuery(id+"F16.boolean.opBoolean","INTERSECT",EDGE,{"derivedFrom":[subQ0,makeQuery(id+"F16.opExtrude","SWEPT_FACE",FACE,{"disambiguationData":[OSD([sQuery(id+"F15.wireOp",EDGE,"E105.MirrorCS")])]})]}),makeQuery(id+"F16.boolean.opBoolean","INTERSECT",EDGE,{"derivedFrom":[subQ0,makeQuery(id+"F16.opExtrude","SWEPT_FACE",FACE,{"disambiguationData":[OSD([sQuery(id+"F15.wireOp",EDGE,"E108.MirrorCS")])]})]})],"blendedInto":[]});}
            var Q9;
            {var subQ0=makeQuery(id+"F1.opExtrude","CAP_FACE",FACE,{"disambiguationData":[OSD([sQuery(id+"F0.wireOp",EDGE,"E0.bottom"),sQuery(id+"F0.wireOp",EDGE,"E0.top"),sQuery(id+"F0.wireOp",EDGE,"E0.left"),sQuery(id+"F0.wireOp",EDGE,"E0.right")])],"isStart":true});Q9=makeQuery(id+"F21.opChamfer","BLEND_EDGE",EDGE,{"blendedFrom":[makeQuery(id+"F16.boolean.opBoolean","INTERSECT",EDGE,{"derivedFrom":[subQ0,makeQuery(id+"F16.opExtrude","SWEPT_FACE",FACE,{"disambiguationData":[OSD([sQuery(id+"F15.wireOp",EDGE,"E108.MirrorCS")])]})]}),subQ0],"blendedInto":[subQ0]});}
            fillet(context, id + "F24", {"entities" : qUnion([Q0, Q1, Q2, Q3, Q4, Q5, Q6, Q7, Q8, Q9]), "radius" : 0.5 * mm, "tangentPropagation" : true, "allowEdgeOverflow" : false});
        }
    });
